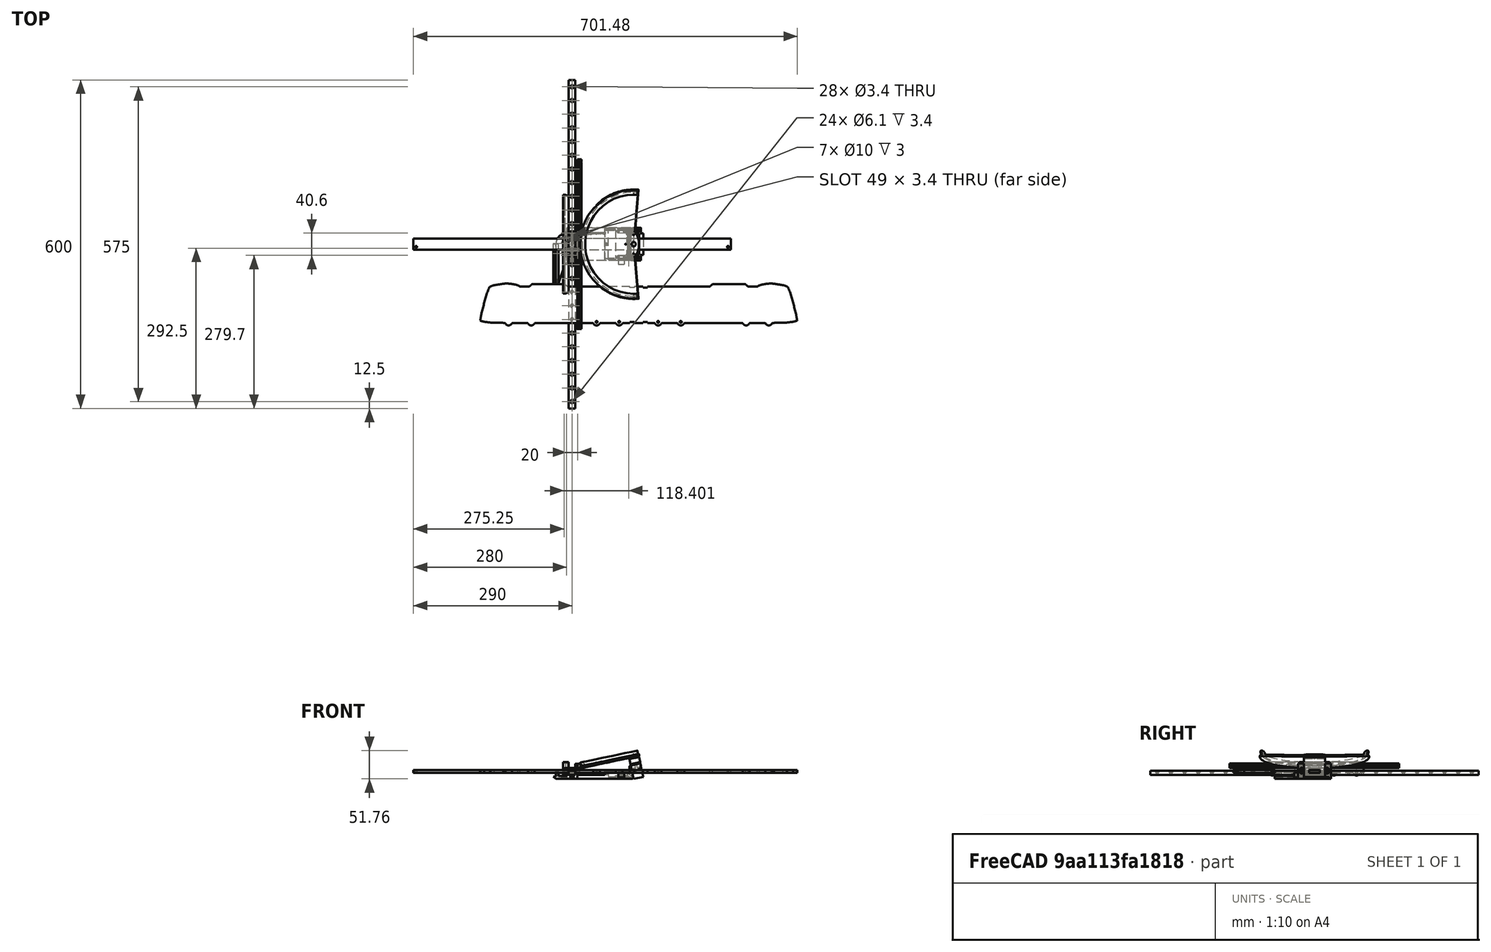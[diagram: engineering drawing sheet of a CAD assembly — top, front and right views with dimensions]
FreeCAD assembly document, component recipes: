
FREECAD ASSEMBLY — COMPONENT RECIPES ("mechanism")

This assembly document has 15 components, labeled P0..P14 below (a component is one placed body or linked part). 14 of them carry a construction recipe — the FreeCAD feature program that regenerates the part from scratch, quoted from this document or its linked companion documents; the rest are supplied as boundary geometry only. No exploded tour is included for this assembly.
NOTE — this tour is split across 2 documents so each fits a 32k-token context. This is document 1: the component sections continue in the remaining 1 document, each repeating the header above.
COMPONENT P0 — recipe-attached ("Block001", modeled in this document).
Construction recipe (the document's own serialized feature program — sketch geometry with constraints, then the solid features built on it; lengths are millimeters unless a unit is written):

FEATURE [PartDesign::SubShapeBinder] Binder  label="SubShapeBinder"
  BindCopyOnChange = 0
  BindMode = 0
  ClaimChildren = false
  Context = -> Body001 [Binder.]
  Fuse = false
  MakeFace = true
  OffsetFill = false
  OffsetIntersection = false
  OffsetJoinType = 0
  OffsetOpenResult = false
  PartialLoad = false
  Refine = true
  Relative = true
  Support = -> [Body[Sketch.]]
  _Version = 2
FEATURE [Sketcher::SketchObject] Sketch001  label="Block Cross-Section"
  ArcFitTolerance = 1e-06
  AttachmentSupport = -> [Binder]
  ExternalGeometry = -> [Binder]
  FullyConstrained = true
  MakeInternals = false
  MapMode = 5
  Placement = pos=(0,0,0) rot=(0,0.707107,0.707107;3.14159rad)
  sketch-geometry (17):
    g0: LineSegment StartX=-13.5 StartY=8.5 StartZ=0 EndX=-13.5 EndY=-0.5 EndZ=0
    g1: LineSegment StartX=-13 StartY=-1 StartZ=0 EndX=-6 EndY=-1 EndZ=0
    g2: LineSegment StartX=13.5 StartY=-0.5 StartZ=0 EndX=13.5 EndY=8.5 EndZ=0
    g3: LineSegment StartX=13 StartY=9 StartZ=0 EndX=-13 EndY=9 EndZ=0
    g4: GeomPoint [constr] X=0 Y=4 Z=0
    g5: LineSegment StartX=-6 StartY=-1 StartZ=0 EndX=-6 EndY=4 EndZ=0
    g6: LineSegment StartX=-6 StartY=4 StartZ=0 EndX=6 EndY=4 EndZ=0
    g7: LineSegment StartX=6 StartY=4 StartZ=0 EndX=6 EndY=-1 EndZ=0
    g8: LineSegment StartX=6 StartY=-1 StartZ=0 EndX=13 EndY=-1 EndZ=0
    g9: ArcOfCircle CenterX=-13 CenterY=8.5 CenterZ=0 NormalX=0 NormalY=0 NormalZ=1 AngleXU=0 Radius=0.5 StartAngle=1.5708 EndAngle=3.14159
    g10: GeomPoint [constr] X=-13.5 Y=9 Z=0
    g11: ArcOfCircle CenterX=13 CenterY=8.5 CenterZ=0 NormalX=0 NormalY=0 NormalZ=1 AngleXU=0 Radius=0.5 StartAngle=-1.8e-15 EndAngle=1.5708
    g12: GeomPoint [constr] X=13.5 Y=9 Z=0
    g13: ArcOfCircle CenterX=13 CenterY=-0.5 CenterZ=0 NormalX=0 NormalY=0 NormalZ=1 AngleXU=0 Radius=0.5 StartAngle=4.71239 EndAngle=6.28319
    g14: GeomPoint [constr] X=13.5 Y=-1 Z=0
    g15: ArcOfCircle CenterX=-13 CenterY=-0.5 CenterZ=0 NormalX=0 NormalY=0 NormalZ=1 AngleXU=0 Radius=0.5 StartAngle=3.14159 EndAngle=4.71239
    g16: GeomPoint [constr] X=-13.5 Y=-1 Z=0
  constraints (41):
    c: Vertical(g0)
    c: Vertical(g2)
    c: Horizontal(g1)
    c: Horizontal(g3)
    c: Symmetric(g14,g10,g4)
    c: PointOnObject(g4,g-2)
    c: Vertical(g5)
    c: Coincident(g5,g6)
    c: Coincident(g6,g7)
    c: PointOnObject(g7,g8)
    c: Vertical(g7)
    c: Coincident(g1,g5)
    c: PointOnObject(g8,g7)
    c: Symmetric(g6,g5,g-2)
    c: PointOnObject(g1,g-3)
    c: PointOnObject(g5,g-4)
    c: DistanceY(g-5,g10) = 13  'Height'
    c: DistanceY(g-5,g16) = 3  'H1'
    c: Horizontal(g7,g1)
    c: Horizontal(g8)
    c: DistanceX(g10,g12) = 27  'W'
    c: PointOnObject(g10,g0)
    c: PointOnObject(g10,g3)
    c: Tangent(g0,g9) = -1.5708
    c: Tangent(g3,g9) = -1.5708
    c: PointOnObject(g12,g3)
    c: PointOnObject(g12,g2)
    c: Tangent(g3,g11) = -1.5708
    c: Tangent(g2,g11) = -1.5708
    c: PointOnObject(g14,g8)
    c: PointOnObject(g14,g2)
    c: Tangent(g8,g13) = -1.5708
    c: Tangent(g2,g13) = -1.5708
    c: PointOnObject(g16,g1)
    c: PointOnObject(g16,g0)
    c: Tangent(g1,g15) = -1.5708
    c: Tangent(g0,g15) = -1.5708
    c: Equal(g9,g15)
    c: Equal(g15,g11)
    c: Equal(g11,g13)
    c: Radius(g9) = 0.5
FEATURE [PartDesign::Pad] Pad001
  Direction = (0,1,-2e-16)
  Length = 32.4
  Length2 = 10
  Midplane = true
  Profile = -> Sketch001
  ReferenceAxis = -> Sketch001 [N_Axis]
  Refine = true
  Suppressed = false
  Type = 0
FEATURE [Sketcher::SketchObject] Sketch002
  ArcFitTolerance = 1e-06
  AttachmentSupport = -> [XZ_Plane001]
  ExternalGeometry = -> [Sketch001]
  FullyConstrained = true
  MakeInternals = false
  MapMode = 5
  Placement = pos=(0,0,0) rot=(1,0,0;1.5708rad)
  sketch-geometry (8):
    g0: LineSegment StartX=-13 StartY=8.5 StartZ=0 EndX=-13 EndY=-0.5 EndZ=0
    g1: LineSegment StartX=-13 StartY=-0.5 StartZ=0 EndX=-6 EndY=-0.5 EndZ=0
    g2: LineSegment StartX=-6 StartY=-0.5 StartZ=0 EndX=-6 EndY=4 EndZ=0
    g3: LineSegment StartX=-6 StartY=4 StartZ=0 EndX=6 EndY=4 EndZ=0
    g4: LineSegment StartX=6 StartY=4 StartZ=0 EndX=6 EndY=-0.5 EndZ=0
    g5: LineSegment StartX=6 StartY=-0.5 StartZ=0 EndX=13 EndY=-0.5 EndZ=0
    g6: LineSegment StartX=13 StartY=-0.5 StartZ=0 EndX=13 EndY=8.5 EndZ=0
    g7: LineSegment StartX=13 StartY=8.5 StartZ=0 EndX=-13 EndY=8.5 EndZ=0
  constraints (22):
    c: Vertical(g0)
    c: Coincident(g0,g1)
    c: PointOnObject(g1,g-7)
    c: Horizontal(g1)
    c: Coincident(g1,g2)
    c: Coincident(g2,g-7)
    c: Coincident(g2,g3)
    c: Coincident(g3,g-6)
    c: Coincident(g3,g4)
    c: Coincident(g4,g5)
    c: Horizontal(g5)
    c: Coincident(g5,g6)
    c: Vertical(g6)
    c: Coincident(g6,g7)
    c: Coincident(g7,g0)
    c: Horizontal(g7)
    c: Vertical(g-3,g0)
    c: Horizontal(g0,g-4)
    c: Horizontal(g-4,g0)
    c: Vertical(g4)
    c: Horizontal(g5,g-5)
    c: Vertical(g-3,g6)
FEATURE [PartDesign::Pad] Pad002  label="BlockExtent"
  BaseFeature = -> Pad001
  Direction = (0,-1,2e-16)
  Length = 45.4
  Length2 = 10
  Midplane = true
  Profile = -> Sketch002
  ReferenceAxis = -> Sketch002 [N_Axis]
  Refine = true
  Suppressed = false
  Type = 0
FEATURE [Sketcher::SketchObject] Sketch004
  ArcFitTolerance = 1e-06
  AttachmentSupport = -> [Pad001]
  FullyConstrained = false
  MakeInternals = false
  MapMode = 5
  Placement = pos=(0,2e-15,9) rot=(0,0,1;0rad)
  sketch-geometry (9):
    g0: Circle CenterX=-10 CenterY=10 CenterZ=0 NormalX=0 NormalY=0 NormalZ=1 AngleXU=0 Radius=2.53403
    g1: Circle CenterX=10 CenterY=10 CenterZ=0 NormalX=0 NormalY=0 NormalZ=1 AngleXU=0 Radius=2.44373
    g2: Circle CenterX=-10 CenterY=-10 CenterZ=0 NormalX=0 NormalY=0 NormalZ=1 AngleXU=0 Radius=2.20024
    g3: Circle CenterX=10 CenterY=-10 CenterZ=0 NormalX=0 NormalY=0 NormalZ=1 AngleXU=0 Radius=2.23133
    g4: LineSegment [constr] StartX=-10 StartY=10 StartZ=0 EndX=-10 EndY=-10 EndZ=0
    g5: LineSegment [constr] StartX=-10 StartY=-10 StartZ=0 EndX=10 EndY=-10 EndZ=0
    g6: LineSegment [constr] StartX=10 StartY=-10 StartZ=0 EndX=10 EndY=10 EndZ=0
    g7: LineSegment [constr] StartX=10 StartY=10 StartZ=0 EndX=-10 EndY=10 EndZ=0
    g8: GeomPoint [constr] X=0 Y=0 Z=0
  constraints (16):
    c: Coincident(g4,g5)
    c: Coincident(g5,g6)
    c: Coincident(g6,g7)
    c: Coincident(g7,g4)
    c: Vertical(g4)
    c: Vertical(g6)
    c: Horizontal(g5)
    c: Horizontal(g7)
    c: Symmetric(g6,g4,g8)
    c: Coincident(g8,g-1)
    c: DistanceX(g7,g7) = 20  'B'
    c: DistanceY(g6,g6) = 20  'C'
    c: Coincident(g0,g4)
    c: Coincident(g1,g6)
    c: Coincident(g5,g3)
    c: Coincident(g4,g2)
FEATURE [PartDesign::Hole] Hole
  BaseFeature = -> Pad002
  CustomThreadClearance = 0
  Depth = 3.5
  DepthType = 0
  Diameter = 2.5
  DrillForDepth = false
  DrillPoint = 1
  DrillPointAngle = 118
  HoleCutCountersinkAngle = 90
  HoleCutCustomValues = false
  HoleCutDepth = 0
  HoleCutDiameter = 6.1
  HoleCutType = 0
  ModelThread = false
  Profile = -> Sketch004
  Refine = true
  Suppressed = false
  Tapered = false
  TaperedAngle = 90
  ThreadClass = 0
  ThreadDepth = 3.5
  ThreadDepthType = 0
  ThreadDirection = 0
  ThreadFit = 0
  ThreadSize = 9
  ThreadType = 1
  Threaded = true
  UseCustomThreadClearance = false
FEATURE [PartDesign::Body] Body001  label="Block"
  AllowCompound = false
  Group = -> [Binder,Sketch001,Pad001,Sketch002,Pad002,Sketch004,Hole]
  Origin = -> Origin001
  Tip = -> Hole
COMPONENT P1 — recipe-attached ("CountdownBracket001", modeled in this document).
Construction recipe (the document's own serialized feature program — sketch geometry with constraints, then the solid features built on it; lengths are millimeters unless a unit is written):

FEATURE [PartDesign::FeatureBase] Clone
  BaseFeature = -> Mirrored
  Placement = pos=(0,0,0) rot=(1,0,0;1.5708rad)
  Suppressed = false
FEATURE [Sketcher::SketchObject] Sketch056
  ArcFitTolerance = 1e-06
  AttachmentSupport = -> [XZ_Plane012]
  FullyConstrained = true
  MakeInternals = false
  MapMode = 5
  Placement = pos=(0,0,0) rot=(1,0,0;1.5708rad)
  sketch-geometry (10):
    g0: LineSegment StartX=-1.7 StartY=-5.97022 StartZ=0 EndX=-2.9 EndY=-6.52978 EndZ=0
    g1: LineSegment StartX=-2.9 StartY=-6.52978 StartZ=0 EndX=-2.9 EndY=-9.02978 EndZ=0
    g2: LineSegment StartX=-2.9 StartY=-9.02978 StartZ=0 EndX=-1.7 EndY=-9.02978 EndZ=0
    g3: LineSegment StartX=1.7 StartY=-9.02978 StartZ=0 EndX=2.9 EndY=-9.02978 EndZ=0
    g4: LineSegment StartX=2.9 StartY=-9.02978 StartZ=0 EndX=2.9 EndY=-6.52978 EndZ=0
    g5: LineSegment StartX=2.9 StartY=-6.52978 StartZ=0 EndX=1.7 EndY=-5.97022 EndZ=0
    g6: LineSegment StartX=1.7 StartY=-5.97022 StartZ=0 EndX=-1.7 EndY=-5.97022 EndZ=0
    g7: LineSegment StartX=-1.7 StartY=-9.02978 StartZ=0 EndX=1.7 EndY=-9.02978 EndZ=0
    g8: LineSegment [constr] StartX=1.7 StartY=-5.97022 StartZ=0 EndX=1.7 EndY=-4 EndZ=0
    g9: LineSegment [constr] StartX=1.7 StartY=-9.02978 StartZ=0 EndX=1.7 EndY=-11 EndZ=0
  constraints (28):
    c: PointOnObject(g0,g-3)
    c: Coincident(g0,g1)
    c: Vertical(g1)
    c: Coincident(g1,g2)
    c: Horizontal(g2)
    c: PointOnObject(g2,g-3)
    c: PointOnObject(g3,g-4)
    c: Horizontal(g3)
    c: Coincident(g3,g4)
    c: Vertical(g4)
    c: Coincident(g4,g5)
    c: PointOnObject(g5,g-4)
    c: Coincident(g5,g6)
    c: Coincident(g6,g0)
    c: Horizontal(g6)
    c: Horizontal(g2,g3)
    c: Equal(g1,g4)
    c: Equal(g0,g5)
    c: Angle(g-4,g5) = 1.13446
    c: DistanceY(g1,g1) = 2.5
    c: Distance(g4,g1) = 5.8
    c: Coincident(g7,g2)
    c: Coincident(g7,g3)
    c: Coincident(g8,g5)
    c: Coincident(g8,g-4)
    c: Coincident(g9,g3)
    c: Coincident(g9,g-4)
    c: Equal(g9,g8)
FEATURE [PartDesign::SubShapeBinder] Binder024  label="CarriageBinder"
  BindCopyOnChange = 0
  BindMode = 0
  ClaimChildren = false
  Context = -> Body011 [Binder024.]
  Fuse = false
  MakeFace = true
  OffsetFill = false
  OffsetIntersection = false
  OffsetJoinType = 0
  OffsetOpenResult = false
  PartialLoad = false
  Refine = true
  Relative = true
  Support = -> [Body003[Pocket.Face11]]
  _Version = 2
FEATURE [PartDesign::SubShapeBinder] Binder025  label="TramBinder"
  BindCopyOnChange = 0
  BindMode = 0
  ClaimChildren = false
  Context = -> Body011 [Binder025.]
  Fuse = false
  MakeFace = true
  OffsetFill = false
  OffsetIntersection = false
  OffsetJoinType = 0
  OffsetOpenResult = false
  PartialLoad = false
  Placement = pos=(0,-217,0) rot=(0,0,1;0rad)
  Refine = true
  Relative = true
  Support = -> [Body003[Sketch052.]]
  _Version = 2
FEATURE [Sketcher::SketchObject] Sketch057  label="CountdownShapeBack"
  ArcFitTolerance = 1e-06
  AttachmentOffset = pos=(0,0,13) rot=(0,0,1;0rad)
  AttachmentSupport = -> [Binder024]
  ExternalGeometry = -> [Binder025]
  FullyConstrained = true
  MakeInternals = false
  MapMode = 5
  Placement = pos=(-29.5,0,0) rot=(0.57735,-0.57735,-0.57735;2.0944rad)
  sketch-geometry (5):
    g0: LineSegment StartX=-72.6664 StartY=12.9462 StartZ=0 EndX=-72.6664 EndY=-7.05384 EndZ=0
    g1: LineSegment StartX=-72.6664 StartY=-7.05384 StartZ=0 EndX=507.334 EndY=-7.05384 EndZ=0
    g2: LineSegment StartX=507.334 StartY=-7.05384 StartZ=0 EndX=507.334 EndY=12.9462 EndZ=0
    g3: LineSegment StartX=507.334 StartY=12.9462 StartZ=0 EndX=-72.6664 EndY=12.9462 EndZ=0
    g4: Circle CenterX=-67.6664 CenterY=-2.05384 CenterZ=0 NormalX=0 NormalY=0 NormalZ=1 AngleXU=0 Radius=1.7
  constraints (15):
    c: Coincident(g0,g1)
    c: Coincident(g1,g2)
    c: Coincident(g2,g3)
    c: Coincident(g3,g0)
    c: Vertical(g0)
    c: Vertical(g2)
    c: Horizontal(g1)
    c: Horizontal(g3)
    c: Distance(g0,g0) = 20
    c: DistanceX(g3,g3) = 580
    c: PointOnObject(g-3,g3)
    c: PointOnObject(g-4,g0)
    c: Diameter(g4) = 3.4
    c: Distance(g4,g0) = 5
    c: Distance(g4,g1) = 5
FEATURE [PartDesign::Pad] Pad024
  BaseFeature = -> Clone
  Direction = (0,1,-3e-16)
  Length = 30
  Length2 = 10
  Placement = pos=(0,0,0) rot=(1,0,0;1.5708rad)
  Profile = -> Clone [Face12]
  Refine = true
  Suppressed = false
  Type = 0
FEATURE [Sketcher::SketchObject] Sketch055
  ArcFitTolerance = 1e-06
  AttachmentSupport = -> [Pad024]
  ExternalGeometry = -> [Pad024]
  FullyConstrained = true
  MakeInternals = false
  MapMode = 5
  Placement = pos=(0,-1.9e-15,-4) rot=(0,0,1;3.14159rad)
  sketch-geometry (6):
    g0: ArcOfCircle CenterX=0 CenterY=15.3 CenterZ=0 NormalX=0 NormalY=0 NormalZ=1 AngleXU=0 Radius=1.7 StartAngle=0 EndAngle=3.14159
    g1: ArcOfCircle CenterX=1.07e-14 CenterY=-30.3 CenterZ=0 NormalX=0 NormalY=0 NormalZ=1 AngleXU=0 Radius=1.7 StartAngle=3.14159 EndAngle=6.28319
    g2: LineSegment StartX=1.7 StartY=15.3 StartZ=0 EndX=1.7 EndY=-30.3 EndZ=0
    g3: LineSegment StartX=-1.7 StartY=15.3 StartZ=0 EndX=-1.7 EndY=-30.3 EndZ=0
    g4: GeomPoint X=0 Y=17 Z=0
    g5: GeomPoint X=0 Y=-32 Z=0
  constraints (14):
    c: Tangent(g0,g2) = 1.5708
    c: Tangent(g0,g3) = -1.5708
    c: Tangent(g1,g2) = 1.5708
    c: Tangent(g1,g3) = -1.5708
    c: Equal(g0,g1)
    c: Vertical(g3)
    c: PointOnObject(g0,g-2)
    c: Diameter(g0) = 3.4
    c: PointOnObject(g4,g0)
    c: PointOnObject(g5,g1)
    c: PointOnObject(g4,g-2)
    c: PointOnObject(g5,g-2)
    c: Distance(g4,g-3) = 3
    c: Distance(g5,g-4) = 3
FEATURE [PartDesign::Pocket] Pocket018  label="ScrewSlot"
  BaseFeature = -> Pad024
  Direction = (0,0,-1)
  Length = 5
  Length2 = 5
  Placement = pos=(0,0,0) rot=(1,0,0;1.5708rad)
  Profile = -> Sketch055
  ReferenceAxis = -> Sketch055 [N_Axis]
  Refine = true
  Suppressed = false
  Type = 1
FEATURE [PartDesign::Pocket] Pocket019  label="NutSlot"
  BaseFeature = -> Pocket018
  Direction = (0,1,-2e-16)
  Length = 0
  Length2 = 5
  Midplane = true
  Placement = pos=(0,0,0) rot=(1,0,0;1.5708rad)
  Profile = -> Sketch056
  ReferenceAxis = -> Sketch056 [N_Axis]
  Refine = true
  Suppressed = false
  Type = 1
FEATURE [Sketcher::SketchObject] Sketch058
  ArcFitTolerance = 1e-06
  AttachmentSupport = -> [Pocket019]
  ExternalGeometry = -> [Sketch057,Binder025,Pocket019]
  FullyConstrained = true
  MakeInternals = false
  MapMode = 5
  Placement = pos=(0,-5.4e-15,-11) rot=(1,0,0;3.14159rad)
  sketch-geometry (11):
    g0: LineSegment StartX=-29.5 StartY=-72.6664 StartZ=0 EndX=-26.4004 EndY=-72.6664 EndZ=0
    g1: LineSegment StartX=-29.5 StartY=-72.6664 StartZ=0 EndX=-29.5 EndY=0.2 EndZ=0
    g2: ArcOfCircle CenterX=-9.7 CenterY=0.2 CenterZ=0 NormalX=0 NormalY=0 NormalZ=1 AngleXU=0 Radius=19.8 StartAngle=1.5708 EndAngle=3.14159
    g3: ArcOfCircle CenterX=-26.4004 CenterY=-70.6664 CenterZ=0 NormalX=0 NormalY=0 NormalZ=1 AngleXU=0 Radius=2 StartAngle=4.71239 EndAngle=5.96626
    g4: LineSegment StartX=-24.5 StartY=-71.2897 StartZ=0 EndX=-13.5008 EndY=-37.7534 EndZ=0
    g5: ArcOfCircle CenterX=-9.7 CenterY=-39 CenterZ=0 NormalX=0 NormalY=0 NormalZ=1 AngleXU=0 Radius=4 StartAngle=1.5708 EndAngle=2.82467
    g6: LineSegment [constr] StartX=-16.5 StartY=-72.6664 StartZ=0 EndX=-16.5 EndY=74.3613 EndZ=0
    g7: LineSegment [constr] StartX=-16.5 StartY=74.3613 StartZ=0 EndX=-21.5 EndY=74.3613 EndZ=0
    g8: LineSegment [constr] StartX=-21.5 StartY=74.3613 StartZ=0 EndX=-21.5 EndY=-72.6664 EndZ=0
    g9: LineSegment [constr] StartX=-21.5 StartY=-72.6664 StartZ=0 EndX=-16.5 EndY=-72.6664 EndZ=0
    g10: LineSegment StartX=-9.7 StartY=20 StartZ=0 EndX=-9.7 EndY=-35 EndZ=0
  constraints (27):
    c: Coincident(g0,g-4)
    c: Horizontal(g0)
    c: Coincident(g1,g0)
    c: Tangent(g1,g2) = 1.5708
    c: Tangent(g0,g3) = -1.5708
    c: Radius(g3) = 2
    c: DistanceX(g0,g3) = 5
    c: PointOnObject(g1,g-4)
    c: Tangent(g5,g4) = 1.5708
    c: Coincident(g6,g7)
    c: Coincident(g7,g8)
    c: Coincident(g8,g9)
    c: Coincident(g9,g6)
    c: Vertical(g8)
    c: Horizontal(g7)
    c: Horizontal(g9)
    c: Distance(g6,g8) = 5
    c: Coincident(g6,g-5)
    c: Coincident(g6,g-6)
    c: Tangent(g4,g3) = -1.5708
    c: Radius(g5) = 4
    c: Coincident(g-7,g2)
    c: PointOnObject(g2,g-7)
    c: Coincident(g5,g-7)
    c: Vertical(g5,g5)
    c: Coincident(g10,g5)
    c: Coincident(g2,g10)
FEATURE [PartDesign::Pad] Pad021  label="Arm"
  BaseFeature = -> Pocket019
  Direction = (0,0,-1)
  Length = 10
  Length2 = 10
  Placement = pos=(0,0,0) rot=(1,0,0;1.5708rad)
  Profile = -> Sketch058
  ReferenceAxis = -> Sketch058 [N_Axis]
  Refine = true
  Suppressed = false
  Type = 3
  UpToFace = -> Pocket019 [Face18]
FEATURE [Sketcher::SketchObject] Sketch059
  ArcFitTolerance = 1e-06
  AttachmentSupport = -> [Pad021]
  ExternalGeometry = -> [Pad021]
  FullyConstrained = true
  MakeInternals = false
  MapMode = 5
  Placement = pos=(0,-2.6e-15,-5.97022) rot=(0,0,1;3.14159rad)
  sketch-geometry (7):
    g0: LineSegment StartX=29.5 StartY=0.2 StartZ=0 EndX=29.5 EndY=-72.6664 EndZ=0
    g1: LineSegment StartX=29.5 StartY=-72.6664 StartZ=0 EndX=26.4004 EndY=-72.6664 EndZ=0
    g2: LineSegment StartX=24.5 StartY=-71.2897 StartZ=0 EndX=24.5 EndY=-1.8 EndZ=0
    g3: LineSegment StartX=26.5 StartY=0.2 StartZ=0 EndX=29.5 EndY=0.2 EndZ=0
    g4: ArcOfCircle CenterX=26.4004 CenterY=-70.6664 CenterZ=0 NormalX=0 NormalY=0 NormalZ=1 AngleXU=0 Radius=2 StartAngle=3.45852 EndAngle=4.71239
    g5: ArcOfCircle CenterX=26.5 CenterY=-1.8 CenterZ=0 NormalX=0 NormalY=0 NormalZ=1 AngleXU=0 Radius=2 StartAngle=1.5708 EndAngle=3.14159
    g6: GeomPoint [constr] X=24.5 Y=0.2 Z=0
  constraints (17):
    c: Coincident(g0,g1)
    c: Vertical(g2)
    c: Coincident(g3,g0)
    c: Horizontal(g3)
    c: Coincident(g4,g1)
    c: Coincident(g4,g2)
    c: PointOnObject(g6,g2)
    c: PointOnObject(g6,g3)
    c: Tangent(g2,g5) = 1.5708
    c: Tangent(g3,g5) = 1.5708
    c: Equal(g5,g4)
    c: Vertical(g0)
    c: Horizontal(g1)
    c: Equal(g4,g-4)
    c: Coincident(g1,g-4)
    c: Coincident(g2,g-4)
    c: Coincident(g0,g-3)
FEATURE [PartDesign::Pad] Pad022
  BaseFeature = -> Pad021
  Direction = (0,0,1)
  Length = 9
  Length2 = 10
  Placement = pos=(0,0,0) rot=(1,0,0;1.5708rad)
  Profile = -> Sketch059
  ReferenceAxis = -> Sketch059 [N_Axis]
  Refine = true
  Suppressed = false
  Type = 0
FEATURE [Sketcher::SketchObject] Sketch060
  ArcFitTolerance = 1e-06
  AttachmentSupport = -> [Pad022]
  ExternalGeometry = -> [Sketch057]
  FullyConstrained = true
  MakeInternals = false
  MapMode = 5
  Placement = pos=(-29.5,0,0) rot=(0.707107,0,-0.707107;3.14159rad)
  sketch-geometry (1):
    g0: Circle CenterX=2.05384 CenterY=-67.6664 CenterZ=0 NormalX=0 NormalY=0 NormalZ=1 AngleXU=0 Radius=1.7
  constraints (2):
    c: Coincident(g0,g-3)
    c: Equal(g0,g-3)
FEATURE [PartDesign::Hole] Hole012
  BaseFeature = -> Pad022
  CustomThreadClearance = 0
  Depth = 222.393
  DepthType = 1
  Diameter = 3.4
  DrillForDepth = false
  DrillPoint = 1
  DrillPointAngle = 118
  HoleCutCountersinkAngle = 90
  HoleCutCustomValues = false
  HoleCutDepth = 0
  HoleCutDiameter = 6.1
  HoleCutType = 0
  ModelThread = false
  Placement = pos=(0,0,0) rot=(1,0,0;1.5708rad)
  Profile = -> Sketch060
  Refine = true
  Suppressed = false
  Tapered = false
  TaperedAngle = 90
  ThreadClass = 0
  ThreadDepth = 222.393
  ThreadDepthType = 0
  ThreadDirection = 0
  ThreadFit = 0
  ThreadSize = 9
  ThreadType = 1
  Threaded = false
  UseCustomThreadClearance = false
FEATURE [Sketcher::SketchObject] Sketch061
  ArcFitTolerance = 1e-06
  AttachmentSupport = -> [Hole012]
  ExternalGeometry = -> [Sketch057]
  FullyConstrained = true
  MakeInternals = false
  MapMode = 5
  Placement = pos=(0,72.6664,0) rot=(-1,0,0;1.5708rad)
  sketch-geometry (3):
    g0: LineSegment StartX=-29.5 StartY=11 StartZ=0 EndX=-34 EndY=7.05384 EndZ=0
    g1: LineSegment StartX=-34 StartY=7.05384 StartZ=0 EndX=-29.5 EndY=7.05384 EndZ=0
    g2: LineSegment StartX=-29.5 StartY=11 StartZ=0 EndX=-29.5 EndY=7.05384 EndZ=0
  constraints (9):
    c: Coincident(g-3,g0)
    c: Coincident(g0,g1)
    c: PointOnObject(g1,g-3)
    c: Horizontal(g1)
    c: Distance(g1,g1) = 4.5
    c: Angle(g0,g-3) = 0.850877
    c: PointOnObject(g-4,g1)
    c: Coincident(g2,g0)
    c: Coincident(g2,g1)
FEATURE [PartDesign::Pad] Pad023
  BaseFeature = -> Hole012
  Direction = (0,1,2e-16)
  Length = 10
  Length2 = 10
  Placement = pos=(0,0,0) rot=(1,0,0;1.5708rad)
  Profile = -> Sketch061
  ReferenceAxis = -> Sketch061 [N_Axis]
  Refine = true
  Reversed = true
  Suppressed = false
  Type = 3
  UpToFace = -> Hole012 [Face37]
FEATURE [Sketcher::SketchObject] Sketch062
  ArcFitTolerance = 1e-06
  AttachmentSupport = -> [Pad023]
  ExternalGeometry = -> [Pad023]
  FullyConstrained = true
  MakeInternals = false
  MapMode = 5
  Placement = pos=(-24.5,0,0) rot=(0.707107,0,0.707107;3.14159rad)
  sketch-geometry (7):
    g0: LineSegment StartX=-3.78589 StartY=-64.6664 StartZ=0 EndX=-5.51794 EndY=-67.6664 EndZ=0
    g1: LineSegment StartX=-5.51794 StartY=-67.6664 StartZ=0 EndX=-3.78589 EndY=-70.6664 EndZ=0
    g2: LineSegment StartX=-3.78589 StartY=-70.6664 StartZ=0 EndX=-0.321787 EndY=-70.6664 EndZ=0
    g3: LineSegment StartX=-0.321787 StartY=-70.6664 StartZ=0 EndX=1.41026 EndY=-67.6664 EndZ=0
    g4: LineSegment StartX=1.41026 StartY=-67.6664 StartZ=0 EndX=-0.321787 EndY=-64.6664 EndZ=0
    g5: LineSegment StartX=-0.321787 StartY=-64.6664 StartZ=0 EndX=-3.78589 EndY=-64.6664 EndZ=0
    g6: Circle [constr] CenterX=-2.05384 CenterY=-67.6664 CenterZ=0 NormalX=0 NormalY=0 NormalZ=1 AngleXU=0 Radius=3.4641
  constraints (16):
    c: Coincident(g0,g1)
    c: Coincident(g1,g2)
    c: Coincident(g2,g3)
    c: Coincident(g3,g4)
    c: Coincident(g4,g5)
    c: Coincident(g5,g0)
    c: Equal(g0, g1-g5) x5
    c: PointOnObject(g0,g6)
    c: PointOnObject(g1,g6)
    c: PointOnObject(g2,g6)
    c: PointOnObject(g3,g6)
    c: PointOnObject(g4,g6)
    c: PointOnObject(g5,g6)
    c: Coincident(g6,g-3)
    c: Horizontal(g5)
    c: Distance(g2,g5) = 6
FEATURE [PartDesign::Pocket] Pocket020  label="HexNutHole"
  BaseFeature = -> Pad023
  Direction = (-1,0,2e-16)
  Length = 2.5
  Length2 = 5
  Placement = pos=(0,0,0) rot=(1,0,0;1.5708rad)
  Profile = -> Sketch062
  ReferenceAxis = -> Sketch062 [N_Axis]
  Refine = true
  Suppressed = false
  Type = 0
FEATURE [Sketcher::SketchObject] Sketch063
  ArcFitTolerance = 1e-06
  AttachmentSupport = -> [Pocket020]
  ExternalGeometry = -> [Pocket020]
  FullyConstrained = true
  MakeInternals = false
  MapMode = 5
  Placement = pos=(0,-3.2e-15,-11) rot=(1,0,0;3.14159rad)
  expr: Constraints[0] = <<FootPads>>.Constraints.FootDiameter
  sketch-geometry (7):
    g0: Circle CenterX=-14.75 CenterY=1.23011 CenterZ=0 NormalX=0 NormalY=0 NormalZ=1 AngleXU=0 Radius=5
    g1: LineSegment [constr] StartX=-29.5 StartY=0.2 StartZ=0 EndX=0 EndY=0.2 EndZ=0
    g2: Circle CenterX=-14.75 CenterY=-16.8849 CenterZ=0 NormalX=0 NormalY=0 NormalZ=1 AngleXU=0 Radius=5
    g3: GeomPoint X=-14.75 Y=0.2 Z=0
    g4: LineSegment [constr] StartX=-14.75 StartY=1.23011 StartZ=0 EndX=-14.75 EndY=19.3452 EndZ=0
    g5: LineSegment [constr] StartX=-14.75 StartY=1.23011 StartZ=0 EndX=-14.75 EndY=-16.8849 EndZ=0
    g6: LineSegment [constr] StartX=-14.75 StartY=-16.8849 StartZ=0 EndX=-14.75 EndY=-35 EndZ=0
  constraints (18):
    c: Diameter(g0) = 10
    c: Horizontal(g1)
    c: PointOnObject(g1,g-2)
    c: Symmetric(g1,g1,g3)
    c: Vertical(g3,g2)
    c: Vertical(g0,g3)
    c: Equal(g0,g2)
    c: Coincident(g4,g0)
    c: Vertical(g4)
    c: Coincident(g5,g0)
    c: Coincident(g5,g2)
    c: Coincident(g6,g2)
    c: Vertical(g6)
    c: Equal(g6,g5)
    c: Equal(g6,g4)
    c: Horizontal(g6,g-4)
    c: PointOnObject(g4,g-3)
    c: Coincident(g1,g-3)
FEATURE [PartDesign::Pocket] Pocket021  label="FootPad"
  BaseFeature = -> Pocket020
  Direction = (0,0,1)
  Length = 3
  Length2 = 5
  Placement = pos=(0,0,0) rot=(1,0,0;1.5708rad)
  Profile = -> Sketch063
  ReferenceAxis = -> Sketch063 [N_Axis]
  Refine = true
  Suppressed = false
  Type = 0
  expr: Length = <<FootPadPocket>>.Length
FEATURE [PartDesign::Body] Body011  label="CountdownBracketL"
  AllowCompound = false
  Group = -> [Clone,Pad024,Sketch055,Pocket018,Sketch056,Pocket019,Binder024,Sketch057,Binder025,Sketch058,Pad021,Sketch059,Pad022,Sketch060,Hole012,Sketch061,Pad023,Sketch062,Pocket020,Sketch063,Pocket021]
  Origin = -> Origin012
  Tip = -> Pocket021
COMPONENT P2 — geometry summary ("CountdownBracketOtherEnd001"; no construction recipe available for this part):
  bounding box: 92.7 x 43.7 x 14.0 mm
  tessellated surface: 2,048 triangles
  volume: 16868 mm^3 (30% of its bounding box)
COMPONENT P3 — recipe-attached ("CountdownPlaceholder001", modeled in this document).
Construction recipe (the document's own serialized feature program — sketch geometry with constraints, then the solid features built on it; lengths are millimeters unless a unit is written):

FEATURE [Sketcher::SketchObject] Sketch067
  ArcFitTolerance = 1e-06
  AttachmentSupport = -> [XY_Plane015]
  FullyConstrained = true
  MakeInternals = false
  MapMode = 5
  sketch-geometry (15):
    g0: LineSegment StartX=-290 StartY=-10 StartZ=0 EndX=290 EndY=-10 EndZ=0
    g1: LineSegment StartX=290 StartY=-10 StartZ=0 EndX=290 EndY=10 EndZ=0
    g2: LineSegment StartX=290 StartY=10 StartZ=0 EndX=-290 EndY=10 EndZ=0
    g3: LineSegment StartX=-290 StartY=10 StartZ=0 EndX=-290 EndY=-10 EndZ=0
    g4: GeomPoint [constr] X=0 Y=0 Z=0
    g5: LineSegment [constr] StartX=-290 StartY=-10 StartZ=0 EndX=-285 EndY=-10 EndZ=0
    g6: LineSegment [constr] StartX=-285 StartY=-10 StartZ=0 EndX=-285 EndY=-5 EndZ=0
    g7: LineSegment [constr] StartX=-285 StartY=-5 StartZ=0 EndX=-290 EndY=-5 EndZ=0
    g8: LineSegment [constr] StartX=-290 StartY=-5 StartZ=0 EndX=-290 EndY=-10 EndZ=0
    g9: LineSegment [constr] StartX=290 StartY=-10 StartZ=0 EndX=290 EndY=-5 EndZ=0
    g10: LineSegment [constr] StartX=290 StartY=-5 StartZ=0 EndX=285 EndY=-5 EndZ=0
    g11: LineSegment [constr] StartX=285 StartY=-5 StartZ=0 EndX=285 EndY=-10 EndZ=0
    g12: LineSegment [constr] StartX=285 StartY=-10 StartZ=0 EndX=290 EndY=-10 EndZ=0
    g13: Circle CenterX=-285 CenterY=-5 CenterZ=0 NormalX=0 NormalY=0 NormalZ=1 AngleXU=0 Radius=1.75
    g14: Circle CenterX=285 CenterY=-5 CenterZ=0 NormalX=0 NormalY=0 NormalZ=1 AngleXU=0 Radius=1.75
  constraints (38):
    c: Coincident(g0,g1)
    c: Coincident(g1,g2)
    c: Coincident(g2,g3)
    c: Coincident(g3,g0)
    c: Horizontal(g0)
    c: Horizontal(g2)
    c: Vertical(g1)
    c: Vertical(g3)
    c: Symmetric(g2,g0,g4)
    c: Distance(g1,g3) = 580
    c: Distance(g0,g2) = 20
    c: Coincident(g4,g-1)
    c: Coincident(g5,g6)
    c: Coincident(g6,g7)
    c: Coincident(g7,g8)
    c: Coincident(g8,g5)
    c: Horizontal(g5)
    c: Horizontal(g7)
    c: Vertical(g6)
    c: Vertical(g8)
    c: Distance(g6,g8) = 5
    c: Distance(g5,g7) = 5
    c: Coincident(g5,g0)
    c: Coincident(g9,g10)
    c: Coincident(g10,g11)
    c: Coincident(g11,g12)
    c: Coincident(g12,g9)
    c: Vertical(g9)
    c: Vertical(g11)
    c: Horizontal(g10)
    c: Horizontal(g12)
    c: Distance(g9,g11) = 5
    c: Distance(g10,g12) = 5
    c: Coincident(g9,g0)
    c: Diameter(g13) = 3.5
    c: Coincident(g13,g6)
    c: Diameter(g14) = 3.5
    c: Coincident(g14,g10)
FEATURE [PartDesign::Pad] Pad026
  Direction = (0,0,1)
  Length = 5
  Length2 = 10
  Profile = -> Sketch067
  ReferenceAxis = -> Sketch067 [N_Axis]
  Refine = true
  Suppressed = false
  Type = 0
FEATURE [PartDesign::Body] Body013  label="CountdownPlaceholder"
  AllowCompound = false
  Group = -> [Sketch067,Pad026]
  Origin = -> Origin015
  Tip = -> Pad026
COMPONENT P4 — recipe-attached ("ElectronicsLid001", modeled in this document).
Construction recipe (the document's own serialized feature program — sketch geometry with constraints, then the solid features built on it; lengths are millimeters unless a unit is written):

FEATURE [PartDesign::SubShapeBinder] Binder018
  BindCopyOnChange = 0
  BindMode = 0
  ClaimChildren = false
  Context = -> Body009 [Binder018.]
  Fuse = false
  MakeFace = true
  OffsetFill = false
  OffsetIntersection = false
  OffsetJoinType = 0
  OffsetOpenResult = false
  PartialLoad = false
  Refine = true
  Relative = true
  Support = -> [Body006[Sketch042.]]
  _Version = 2
FEATURE [PartDesign::SubShapeBinder] Binder019
  BindCopyOnChange = 0
  BindMode = 0
  ClaimChildren = false
  Context = -> Body009 [Binder019.]
  Fuse = false
  MakeFace = true
  OffsetFill = false
  OffsetIntersection = false
  OffsetJoinType = 0
  OffsetOpenResult = false
  PartialLoad = false
  Refine = true
  Relative = true
  Support = -> [Body006[Sketch023.]]
  _Version = 2
FEATURE [Sketcher::SketchObject] Sketch046
  ArcFitTolerance = 1e-06
  AttachmentSupport = -> [Binder018]
  ExternalGeometry = -> [Binder018]
  FullyConstrained = true
  MakeInternals = false
  MapMode = 5
  Placement = pos=(100.82,0,0) rot=(0.57735,0.57735,0.57735;2.0944rad)
  sketch-geometry (4):
    g0: LineSegment StartX=-25.8 StartY=4 StartZ=0 EndX=-27.8 EndY=2 EndZ=0
    g1: LineSegment StartX=-27.8 StartY=2 StartZ=0 EndX=27.8 EndY=2 EndZ=0
    g2: LineSegment StartX=27.8 StartY=2 StartZ=0 EndX=25.8 EndY=4 EndZ=0
    g3: LineSegment StartX=25.8 StartY=4 StartZ=0 EndX=-25.8 EndY=4 EndZ=0
  constraints (11):
    c: PointOnObject(g0,g-3)
    c: PointOnObject(g0,g-5)
    c: Coincident(g0,g1)
    c: PointOnObject(g1,g-5)
    c: Coincident(g1,g2)
    c: Coincident(g2,g3)
    c: Coincident(g3,g0)
    c: Equal(g-4,g0)
    c: Equal(g-6,g2)
    c: Symmetric(g0,g2,g-2)
    c: Distance(g2,g-6) = 0.2
FEATURE [PartDesign::Pad] Pad018
  Direction = (1,0,0)
  Length = 1.9
  Length2 = 10
  Profile = -> Sketch046
  ReferenceAxis = -> Sketch046 [N_Axis]
  Refine = true
  Suppressed = false
  Type = 0
  expr: Length = <<LidOvershoot>>.Length - 0.1 mm
FEATURE [PartDesign::SubShapeBinder] Binder020
  BindCopyOnChange = 0
  BindMode = 0
  ClaimChildren = false
  Context = -> Body009 [Binder020.]
  Fuse = false
  MakeFace = true
  OffsetFill = false
  OffsetIntersection = false
  OffsetJoinType = 0
  OffsetOpenResult = false
  PartialLoad = false
  Refine = true
  Relative = true
  Support = -> [Body006[SubtractivePipe.Face17]]
  _Version = 2
FEATURE [PartDesign::Pad] Pad019
  BaseFeature = -> Pad018
  Direction = (1,0,0)
  Length = 10
  Length2 = 10
  Profile = -> Sketch046
  ReferenceAxis = -> Sketch046 [N_Axis]
  Refine = true
  Suppressed = false
  Type = 3
  UpToFace = -> SubtractivePipe [Face17]
FEATURE [PartDesign::SubShapeBinder] Binder022
  BindCopyOnChange = 0
  BindMode = 0
  ClaimChildren = false
  Context = -> Body009 [Binder022.]
  Fuse = false
  MakeFace = true
  OffsetFill = false
  OffsetIntersection = false
  OffsetJoinType = 0
  OffsetOpenResult = false
  PartialLoad = false
  Refine = true
  Relative = true
  Support = -> [Body006[Sketch049.]]
  _Version = 2
FEATURE [Sketcher::SketchObject] Sketch047
  ArcFitTolerance = 1e-06
  AttachmentSupport = -> [Binder019]
  ExternalGeometry = -> [Binder019,Binder022]
  FullyConstrained = true
  MakeInternals = false
  MapMode = 5
  Placement = pos=(0,-6e-16,0) rot=(0,0.707107,0.707107;3.14159rad)
  sketch-geometry (7):
    g0: LineSegment StartX=-61.8197 StartY=4 StartZ=0 EndX=-59.8197 EndY=4 EndZ=0
    g1: LineSegment StartX=-59.8197 StartY=4 StartZ=0 EndX=-59.8197 EndY=2 EndZ=0
    g2: ArcOfCircle CenterX=-61.8197 CenterY=2 CenterZ=0 NormalX=0 NormalY=0 NormalZ=1 AngleXU=0 Radius=2 StartAngle=9.81107e-09 EndAngle=1.5708
    g3: LineSegment StartX=-102.82 StartY=2 StartZ=0 EndX=-102.82 EndY=4 EndZ=0
    g4: LineSegment StartX=-102.82 StartY=4 StartZ=0 EndX=-101.55 EndY=4 EndZ=0
    g5: LineSegment StartX=-101.55 StartY=4 StartZ=0 EndX=-102.704 EndY=2 EndZ=0
    g6: LineSegment StartX=-102.704 StartY=2 StartZ=0 EndX=-102.82 EndY=2 EndZ=0
  constraints (18):
    c: Coincident(g-3,g0)
    c: Coincident(g0,g1)
    c: Coincident(g1,g-3)
    c: Vertical(g1)
    c: Horizontal(g0)
    c: Coincident(g2,g0)
    c: Coincident(g2,g1)
    c: Tangent(g2,g-3)
    c: Coincident(g-5,g3)
    c: Coincident(g3,g-5)
    c: Coincident(g3,g4)
    c: Horizontal(g4)
    c: Coincident(g4,g5)
    c: Coincident(g5,g6)
    c: Coincident(g6,g3)
    c: Horizontal(g6)
    c: Parallel(g-4,g5)
    c: Distance(g5,g-4) = 0.1
FEATURE [PartDesign::Pocket] Pocket016
  BaseFeature = -> Pad019
  Direction = (0,-1,2e-16)
  Length = 5
  Length2 = 5
  Midplane = true
  Profile = -> Sketch047
  ReferenceAxis = -> Sketch047 [N_Axis]
  Refine = true
  Suppressed = false
  Type = 1
FEATURE [PartDesign::SubShapeBinder] Binder023
  BindCopyOnChange = 0
  BindMode = 0
  ClaimChildren = false
  Context = -> Body009 [Binder023.]
  Fuse = false
  MakeFace = true
  OffsetFill = false
  OffsetIntersection = false
  OffsetJoinType = 0
  OffsetOpenResult = false
  PartialLoad = false
  Refine = true
  Relative = true
  Support = -> [Body006[Sketch043.]]
  _Version = 2
FEATURE [Sketcher::SketchObject] Sketch048
  ArcFitTolerance = 1e-06
  AttachmentSupport = -> [Pocket016]
  ExternalGeometry = -> [Binder023]
  FullyConstrained = true
  MakeInternals = false
  MapMode = 5
  Placement = pos=(0,0,4) rot=(0,0,1;0rad)
  sketch-geometry (1):
    g0: Circle CenterX=62.8197 CenterY=0 CenterZ=0 NormalX=0 NormalY=0 NormalZ=1 AngleXU=0 Radius=1.5
  constraints (2):
    c: Coincident(g0,g-3)
    c: Equal(g0,g-3)
FEATURE [PartDesign::Hole] Hole009
  BaseFeature = -> Pocket016
  CustomThreadClearance = 0
  Depth = 141.896
  DepthType = 1
  Diameter = 2.4
  DrillForDepth = false
  DrillPoint = 1
  DrillPointAngle = 118
  HoleCutCountersinkAngle = 90
  HoleCutCustomValues = false
  HoleCutDepth = 1
  HoleCutDiameter = 4
  HoleCutType = 1
  ModelThread = false
  Profile = -> Sketch048
  Refine = true
  Suppressed = false
  Tapered = false
  TaperedAngle = 90
  ThreadClass = 0
  ThreadDepth = 141.896
  ThreadDepthType = 0
  ThreadDirection = 0
  ThreadFit = 0
  ThreadSize = 6
  ThreadType = 1
  Threaded = false
  UseCustomThreadClearance = false
FEATURE [PartDesign::Body] Body009  label="ElectronicsLid"
  AllowCompound = false
  Group = -> [Binder018,Binder019,Sketch046,Pad018,Binder020,Pad019,Sketch047,Pocket016,Sketch048,Hole009,Binder022,Binder023]
  Origin = -> Origin010
  Tip = -> Hole009
COMPONENT P5 — recipe-attached ("Foot001", modeled in this document).
Construction recipe (the document's own serialized feature program — sketch geometry with constraints, then the solid features built on it; lengths are millimeters unless a unit is written):

FEATURE [PartDesign::SubShapeBinder] Binder001
  BindCopyOnChange = 0
  BindMode = 0
  ClaimChildren = false
  Context = -> Body002 [Binder001.]
  Fuse = false
  MakeFace = true
  OffsetFill = false
  OffsetIntersection = false
  OffsetJoinType = 0
  OffsetOpenResult = false
  PartialLoad = false
  Refine = true
  Relative = true
  Support = -> [Body[Sketch.]]
  _Version = 2
FEATURE [PartDesign::SubShapeBinder] Binder002
  BindCopyOnChange = 0
  BindMode = 0
  ClaimChildren = false
  Context = -> Body002 [Binder002.]
  Fuse = false
  MakeFace = true
  OffsetFill = false
  OffsetIntersection = false
  OffsetJoinType = 0
  OffsetOpenResult = false
  PartialLoad = false
  Refine = true
  Relative = true
  Support = -> [Body001[Sketch001.]]
  _Version = 2
FEATURE [Sketcher::SketchObject] Sketch006  label="FootProfile"
  ArcFitTolerance = 1e-06
  AttachmentSupport = -> [XZ_Plane002]
  ExternalGeometry = -> [Binder001,Binder002]
  FullyConstrained = true
  MakeInternals = false
  MapMode = 5
  Placement = pos=(0,0,0) rot=(1,0,0;1.5708rad)
  sketch-geometry (12):
    g0: LineSegment StartX=-9.7 StartY=-4 StartZ=0 EndX=-9.7 EndY=-11 EndZ=0
    g1: LineSegment StartX=-6.1 StartY=-4 StartZ=0 EndX=-6.1 EndY=-2.6 EndZ=0
    g2: LineSegment StartX=-6.7 StartY=-2 StartZ=0 EndX=-7.7 EndY=-2 EndZ=0
    g3: LineSegment StartX=-6.1 StartY=-4 StartZ=0 EndX=0 EndY=-4 EndZ=0
    g4: LineSegment StartX=0 StartY=-4 StartZ=0 EndX=0 EndY=-11 EndZ=0
    g5: LineSegment StartX=0 StartY=-11 StartZ=0 EndX=-9.7 EndY=-11 EndZ=0
    g6: ArcOfCircle [constr] CenterX=-6.7 CenterY=-2.6 CenterZ=0 NormalX=0 NormalY=0 NormalZ=1 AngleXU=0 Radius=0.6 StartAngle=1e-16 EndAngle=1.5708
    g7: GeomPoint [constr] X=-6.1 Y=-2 Z=0
    g8: LineSegment StartX=-6.1 StartY=-2.6 StartZ=0 EndX=-6.7 EndY=-2 EndZ=0
    g9: ArcOfCircle [constr] CenterX=-7.7 CenterY=-4 CenterZ=0 NormalX=0 NormalY=0 NormalZ=1 AngleXU=0 Radius=2 StartAngle=1.5708 EndAngle=3.14159
    g10: GeomPoint [constr] X=-9.7 Y=-2 Z=0
    g11: LineSegment StartX=-7.7 StartY=-2 StartZ=0 EndX=-9.7 EndY=-4 EndZ=0
  constraints (30):
    c: Vertical(g0)
    c: Vertical(g1)
    c: Horizontal(g2)
    c: Distance(g-3,g1) = 0.1
    c: Distance(g-4,g2) = 1
    c: Coincident(g3,g1)
    c: PointOnObject(g3,g-2)
    c: Horizontal(g3)
    c: Coincident(g4,g3)
    c: Vertical(g4)
    c: Coincident(g5,g4)
    c: Coincident(g5,g0)
    c: Horizontal(g5)
    c: Distance(g4,g4) = 7  'BaseThickness'
    c: PointOnObject(g1,g-5)
    c: PointOnObject(g7,g2)
    c: PointOnObject(g7,g1)
    c: Tangent(g2,g6) = -1.5708
    c: Tangent(g1,g6) = -1.5708
    c: Coincident(g8,g2)
    c: Coincident(g8,g1)
    c: PointOnObject(g10,g2)
    c: PointOnObject(g10,g0)
    c: Tangent(g2,g9) = -1.5708
    c: Tangent(g0,g9) = -1.5708
    c: Coincident(g11,g2)
    c: Coincident(g11,g0)
    c: Distance(g1,g7) = 0.6
    c: Distance(g2,g2) = 1
    c: Horizontal(g9,g1)
FEATURE [PartDesign::Pad] Pad003
  Direction = (0,-1,2e-16)
  Length = 20
  Length2 = 5
  Midplane = true
  Placement = pos=(0,0,0) rot=(1,0,0;1.5708rad)
  Profile = -> Sketch006
  ReferenceAxis = -> Sketch006 [N_Axis]
  Refine = true
  Suppressed = false
  Type = 4
FEATURE [PartDesign::Mirrored] Mirrored
  BaseFeature = -> Pad003
  MirrorPlane = -> Sketch006 [V_Axis]
  Originals = -> [Pad003]
  Placement = pos=(0,0,0) rot=(1,0,0;1.5708rad)
  Refine = true
  Suppressed = false
  TransformMode = 0
FEATURE [Sketcher::SketchObject] Sketch007
  ArcFitTolerance = 1e-06
  AttachmentSupport = -> [Mirrored]
  FullyConstrained = false
  MakeInternals = false
  MapMode = 5
  Placement = pos=(0,-1.8e-15,-4) rot=(0,0,1;3.14159rad)
  sketch-geometry (1):
    g0: Circle CenterX=0 CenterY=0 CenterZ=0 NormalX=0 NormalY=0 NormalZ=1 AngleXU=0 Radius=1.1986
  constraints (1):
    c: Coincident(g0,g-1)
FEATURE [PartDesign::Hole] Hole002  label="FootHole"
  BaseFeature = -> Mirrored
  CustomThreadClearance = 0
  Depth = 109.851
  DepthType = 1
  Diameter = 4.4
  DrillForDepth = false
  DrillPoint = 1
  DrillPointAngle = 118
  HoleCutCountersinkAngle = 90
  HoleCutCustomValues = false
  HoleCutDepth = 0
  HoleCutDiameter = 6.1
  HoleCutType = 0
  ModelThread = false
  Placement = pos=(0,0,0) rot=(1,0,0;1.5708rad)
  Profile = -> Sketch007
  Refine = true
  Suppressed = false
  Tapered = false
  TaperedAngle = 90
  ThreadClass = 0
  ThreadDepth = 109.851
  ThreadDepthType = 0
  ThreadDirection = 0
  ThreadFit = 0
  ThreadSize = 0
  ThreadType = 0
  Threaded = false
  UseCustomThreadClearance = false
FEATURE [Sketcher::SketchObject] Sketch028  label="FootPads"
  ArcFitTolerance = 1e-06
  AttachmentSupport = -> [Hole002]
  ExternalGeometry = -> [Hole002]
  FullyConstrained = true
  MakeInternals = false
  MapMode = 5
  Placement = pos=(0,-4.7e-15,-11) rot=(1,0,0;3.14159rad)
  sketch-geometry (3):
    g0: Circle CenterX=0 CenterY=12 CenterZ=0 NormalX=0 NormalY=0 NormalZ=1 AngleXU=0 Radius=5
    g1: GeomPoint X=0 Y=20 Z=0
    g2: GeomPoint X=0 Y=17 Z=0
  constraints (7):
    c: PointOnObject(g0,g-2)
    c: Diameter(g0) = 10  'FootDiameter'
    c: PointOnObject(g1,g-2)
    c: PointOnObject(g2,g0)
    c: PointOnObject(g2,g-2)
    c: Distance(g2,g1) = 3
    c: PointOnObject(g1,g-3)
FEATURE [PartDesign::Pocket] Pocket008  label="FootPadPocket"
  BaseFeature = -> Hole002
  Direction = (0,0,1)
  Length = 3
  Length2 = 5
  Placement = pos=(0,0,0) rot=(1,0,0;1.5708rad)
  Profile = -> Sketch028
  ReferenceAxis = -> Sketch028 [N_Axis]
  Refine = true
  Suppressed = false
  Type = 0
FEATURE [Sketcher::SketchObject] Sketch032  label="FootEndBlock"
  ArcFitTolerance = 1e-06
  AttachmentSupport = -> [Pocket008]
  ExternalGeometry = -> [Pocket008]
  FullyConstrained = true
  MakeInternals = false
  MapMode = 5
  Placement = pos=(0,-1.8e-15,-4) rot=(0,0,1;3.14159rad)
  expr: Constraints[11] = <<RailHolePosition>>.Constraints.E + 1 mm
  sketch-geometry (5):
    g0: LineSegment StartX=-9.7 StartY=20 StartZ=0 EndX=-9.7 EndY=8.5 EndZ=0
    g1: LineSegment StartX=-9.7 StartY=8.5 StartZ=0 EndX=9.7 EndY=8.5 EndZ=0
    g2: LineSegment StartX=9.7 StartY=8.5 StartZ=0 EndX=9.7 EndY=20 EndZ=0
    g3: LineSegment StartX=9.7 StartY=20 StartZ=0 EndX=-9.7 EndY=20 EndZ=0
    g4: LineSegment [constr] StartX=-9.7 StartY=13.5 StartZ=0 EndX=9.7 EndY=13.5 EndZ=0
  constraints (15):
    c: Coincident(g0,g1)
    c: Coincident(g1,g2)
    c: Coincident(g2,g3)
    c: Coincident(g3,g0)
    c: Vertical(g0)
    c: Vertical(g2)
    c: Horizontal(g1)
    c: Horizontal(g3)
    c: PointOnObject(g4,g0)
    c: PointOnObject(g4,g2)
    c: Horizontal(g4)
    c: DistanceY(g-1,g4) = 13.5
    c: DistanceY(g1,g4) = 5  'Overhang'
    c: Vertical(g0,g-3)
    c: Coincident(g-3,g2)
FEATURE [PartDesign::Pad] Pad013
  BaseFeature = -> Pocket008
  Direction = (0,0,1)
  Length = 13
  Length2 = 10
  Placement = pos=(0,0,0) rot=(1,0,0;1.5708rad)
  Profile = -> Sketch032
  ReferenceAxis = -> Sketch032 [N_Axis]
  Refine = true
  Suppressed = false
  Type = 0
  expr: Length = <<Block Cross-Section>>.Constraints.Height
FEATURE [Sketcher::SketchObject] Sketch033
  ArcFitTolerance = 1e-06
  AttachmentSupport = -> [Pad013]
  FullyConstrained = true
  MakeInternals = false
  MapMode = 5
  Placement = pos=(0,-8.5,1.9e-15) rot=(-1,0,0;1.5708rad)
  expr: Constraints[10] = <<Rail Cross-Section>>.Constraints.Hr + 0.5 mm
  sketch-geometry (4):
    g0: LineSegment StartX=-6.1 StartY=4 StartZ=0 EndX=-6.1 EndY=-4.5 EndZ=0
    g1: LineSegment StartX=-6.1 StartY=-4.5 StartZ=0 EndX=6.1 EndY=-4.5 EndZ=0
    g2: LineSegment StartX=6.1 StartY=-4.5 StartZ=0 EndX=6.1 EndY=4 EndZ=0
    g3: LineSegment StartX=6.1 StartY=4 StartZ=0 EndX=-6.1 EndY=4 EndZ=0
  constraints (11):
    c: Coincident(g0,g1)
    c: Coincident(g1,g2)
    c: Coincident(g2,g3)
    c: Coincident(g3,g0)
    c: Vertical(g0)
    c: Vertical(g2)
    c: Horizontal(g1)
    c: Horizontal(g3)
    c: Coincident(g0,g-3)
    c: PointOnObject(g-4,g2)
    c: DistanceY(g2,g2) = 8.5
FEATURE [PartDesign::Pocket] Pocket010
  BaseFeature = -> Pad013
  Direction = (0,-1,-2e-16)
  Length = 5
  Length2 = 5
  Placement = pos=(0,0,0) rot=(1,0,0;1.5708rad)
  Profile = -> Sketch033
  ReferenceAxis = -> Sketch033 [N_Axis]
  Refine = true
  Suppressed = false
  Type = 0
  expr: Length = <<FootEndBlock>>.Constraints.Overhang
FEATURE [PartDesign::Fillet] Fillet004
  Base = -> Pocket010 [Edge24,Edge50,Edge33,Edge25,Edge32]
  BaseFeature = -> Pocket010
  Placement = pos=(0,0,0) rot=(1,0,0;1.5708rad)
  Radius = 5
  Refine = true
  SupportTransform = false
  Suppressed = false
  UseAllEdges = false
FEATURE [PartDesign::Body] Body002  label="Foot"
  AllowCompound = false
  Group = -> [Binder001,Binder002,Sketch006,Pad003,Mirrored,Sketch007,Hole002,Sketch028,Pocket008,Sketch032,Pad013,Sketch033,Pocket010,Fillet004]
  Origin = -> Origin002
  Tip = -> Fillet004
COMPONENT P6 — same part as P5; its construction recipe is shown at P5.
COMPONENT P7 — recipe-attached ("PicoW001", modeled in this document).
Construction recipe (the document's own serialized feature program — sketch geometry with constraints, then the solid features built on it; lengths are millimeters unless a unit is written):

FEATURE [Sketcher::SketchObject] Sketch034
  ArcFitTolerance = 1e-06
  AttachmentSupport = -> [XY_Plane009]
  FullyConstrained = true
  MakeInternals = false
  MapMode = 5
  sketch-geometry (14):
    g0: LineSegment StartX=-10.5 StartY=-25.5 StartZ=0 EndX=10.5 EndY=-25.5 EndZ=0
    g1: LineSegment StartX=10.5 StartY=-25.5 StartZ=0 EndX=10.5 EndY=25.5 EndZ=0
    g2: LineSegment StartX=10.5 StartY=25.5 StartZ=0 EndX=-10.5 EndY=25.5 EndZ=0
    g3: LineSegment StartX=-10.5 StartY=25.5 StartZ=0 EndX=-10.5 EndY=-25.5 EndZ=0
    g4: GeomPoint [constr] X=0 Y=0 Z=0
    g5: LineSegment [constr] StartX=-5.7 StartY=-23.5 StartZ=0 EndX=5.7 EndY=-23.5 EndZ=0
    g6: LineSegment [constr] StartX=5.7 StartY=-23.5 StartZ=0 EndX=5.7 EndY=23.5 EndZ=0
    g7: LineSegment [constr] StartX=5.7 StartY=23.5 StartZ=0 EndX=-5.7 EndY=23.5 EndZ=0
    g8: LineSegment [constr] StartX=-5.7 StartY=23.5 StartZ=0 EndX=-5.7 EndY=-23.5 EndZ=0
    g9: GeomPoint [constr] X=0 Y=0 Z=0
    g10: Circle CenterX=-5.7 CenterY=23.5 CenterZ=0 NormalX=0 NormalY=0 NormalZ=1 AngleXU=0 Radius=1.05
    g11: Circle CenterX=5.7 CenterY=23.5 CenterZ=0 NormalX=0 NormalY=0 NormalZ=1 AngleXU=0 Radius=1.05
    g12: Circle CenterX=-5.7 CenterY=-23.5 CenterZ=0 NormalX=0 NormalY=0 NormalZ=1 AngleXU=0 Radius=1.05
    g13: Circle CenterX=5.7 CenterY=-23.5 CenterZ=0 NormalX=0 NormalY=0 NormalZ=1 AngleXU=0 Radius=1.05
  constraints (32):
    c: Coincident(g0,g1)
    c: Coincident(g1,g2)
    c: Coincident(g2,g3)
    c: Coincident(g3,g0)
    c: Horizontal(g0)
    c: Horizontal(g2)
    c: Vertical(g1)
    c: Vertical(g3)
    c: Symmetric(g2,g0,g4)
    c: Distance(g1,g3) = 21
    c: Distance(g0,g2) = 51  'Height'
    c: Coincident(g4,g-1)
    c: Coincident(g5,g6)
    c: Coincident(g6,g7)
    c: Coincident(g7,g8)
    c: Coincident(g8,g5)
    c: Horizontal(g5)
    c: Horizontal(g7)
    c: Vertical(g6)
    c: Vertical(g8)
    c: Symmetric(g7,g5,g9)
    c: Distance(g6,g8) = 11.4
    c: Coincident(g9,g4)
    c: Distance(g5,g0) = 2
    c: Coincident(g10,g7)
    c: Coincident(g11,g6)
    c: Coincident(g12,g5)
    c: Coincident(g13,g5)
    c: Equal(g10,g11)
    c: Equal(g11,g12)
    c: Equal(g12,g13)
    c: Diameter(g10) = 2.1  'HoleDiameter'
FEATURE [PartDesign::Pad] Pad014  label="Board"
  Direction = (0,0,1)
  Length = 1
  Length2 = 10
  Profile = -> Sketch034
  ReferenceAxis = -> Sketch034 [N_Axis]
  Refine = true
  Suppressed = false
  Type = 0
FEATURE [Sketcher::SketchObject] Sketch035
  ArcFitTolerance = 1e-06
  AttachmentOffset = pos=(0,0,-0.3) rot=(0,0,1;0rad)
  AttachmentSupport = -> [Pad014]
  ExternalGeometry = -> [Pad014]
  FullyConstrained = true
  MakeInternals = false
  MapMode = 5
  Placement = pos=(0,0,0.7) rot=(0,0,1;0rad)
  sketch-geometry (5):
    g0: LineSegment StartX=-4 StartY=26.8 StartZ=0 EndX=-4 EndY=20.8 EndZ=0
    g1: LineSegment StartX=-4 StartY=20.8 StartZ=0 EndX=4 EndY=20.8 EndZ=0
    g2: LineSegment StartX=4 StartY=20.8 StartZ=0 EndX=4 EndY=26.8 EndZ=0
    g3: LineSegment StartX=4 StartY=26.8 StartZ=0 EndX=-4 EndY=26.8 EndZ=0
    g4: GeomPoint X=0 Y=26.8 Z=0
  constraints (13):
    c: Coincident(g0,g1)
    c: Coincident(g1,g2)
    c: Coincident(g2,g3)
    c: Coincident(g3,g0)
    c: Vertical(g0)
    c: Vertical(g2)
    c: Horizontal(g1)
    c: Horizontal(g3)
    c: Distance(g0,g2) = 8
    c: DistanceY(g0,g0) = 6
    c: Distance(g-3,g3) = 1.3
    c: Symmetric(g3,g3,g4)
    c: PointOnObject(g4,g-2)
FEATURE [PartDesign::Pad] Pad015  label="Socket"
  BaseFeature = -> Pad014
  Direction = (0,0,1)
  Length = 3
  Length2 = 10
  Profile = -> Sketch035
  ReferenceAxis = -> Sketch035 [N_Axis]
  Refine = true
  Suppressed = false
  Type = 0
FEATURE [Sketcher::SketchObject] Sketch036
  ArcFitTolerance = 1e-06
  AttachmentSupport = -> [Pad015]
  ExternalGeometry = -> [Pad015]
  FullyConstrained = true
  MakeInternals = false
  MapMode = 5
  Placement = pos=(0,26.8,0) rot=(0,0.707107,0.707107;3.14159rad)
  sketch-geometry (5):
    g0: LineSegment StartX=-5.5 StartY=-2.3 StartZ=0 EndX=5.5 EndY=-2.3 EndZ=0
    g1: LineSegment StartX=5.5 StartY=-2.3 StartZ=0 EndX=5.5 EndY=6.7 EndZ=0
    g2: LineSegment StartX=5.5 StartY=6.7 StartZ=0 EndX=-5.5 EndY=6.7 EndZ=0
    g3: LineSegment StartX=-5.5 StartY=6.7 StartZ=0 EndX=-5.5 EndY=-2.3 EndZ=0
    g4: GeomPoint [constr] X=1e-16 Y=2.2 Z=0
  constraints (12):
    c: Coincident(g0,g1)
    c: Coincident(g1,g2)
    c: Coincident(g2,g3)
    c: Coincident(g3,g0)
    c: Horizontal(g0)
    c: Horizontal(g2)
    c: Vertical(g1)
    c: Vertical(g3)
    c: Symmetric(g2,g0,g4)
    c: Distance(g1,g3) = 11
    c: Distance(g0,g2) = 9
    c: Symmetric(g-3,g-4,g4)
FEATURE [PartDesign::Pad] Pad016  label="Keepout"
  BaseFeature = -> Pad015
  Direction = (0,1,-2e-16)
  Length = 10
  Length2 = 10
  Profile = -> Sketch036
  ReferenceAxis = -> Sketch036 [N_Axis]
  Refine = true
  Suppressed = false
  Type = 0
FEATURE [PartDesign::Body] Body008  label="PicoW"
  AllowCompound = false
  Group = -> [Sketch034,Pad014,Sketch035,Pad015,Sketch036,Pad016]
  Origin = -> Origin009
  Placement = pos=(90,0,-6) rot=(0,0,1;3.14159rad)
  Tip = -> Pad016
COMPONENT P8 — recipe-attached ("Pinion001", modeled in this document).
Construction recipe (the document's own serialized feature program — sketch geometry with constraints, then the solid features built on it; lengths are millimeters unless a unit is written):

FEATURE [PartDesign::SubShapeBinder] Binder010
  BindCopyOnChange = 0
  BindMode = 0
  ClaimChildren = false
  Context = -> Body005 [Binder010.]
  Fuse = false
  MakeFace = true
  OffsetFill = false
  OffsetIntersection = false
  OffsetJoinType = 0
  OffsetOpenResult = false
  PartialLoad = false
  Refine = true
  Relative = true
  Support = -> [Body004[Sketch012.]]
  _Version = 2
FEATURE [PartDesign::SubShapeBinder] Binder011
  BindCopyOnChange = 0
  BindMode = 0
  ClaimChildren = false
  Context = -> Body005 [Binder011.]
  Fuse = false
  MakeFace = true
  OffsetFill = false
  OffsetIntersection = false
  OffsetJoinType = 0
  OffsetOpenResult = false
  PartialLoad = false
  Refine = true
  Relative = true
  Support = -> [Body002[Sketch006.]]
  _Version = 2
FEATURE [Sketcher::SketchObject] Sketch019  label="PinionCrossSection"
  ArcFitTolerance = 1e-06
  AttachmentSupport = -> [XZ_Plane005]
  ExternalGeometry = -> [Binder010,Binder011]
  FullyConstrained = true
  MakeInternals = false
  MapMode = 5
  Placement = pos=(0,0,0) rot=(1,0,0;1.5708rad)
  expr: Constraints[46] = <<RackStringEnds>>.Constraints.Length / pi
  sketch-geometry (27):
    g0: LineSegment StartX=14.9142 StartY=17 StartZ=0 EndX=18.9142 EndY=13 EndZ=0
    g1: LineSegment StartX=18.9142 StartY=13 StartZ=0 EndX=15.2909 EndY=9.37671 EndZ=0
    g2: LineSegment StartX=15.7474 StartY=8.53387 StartZ=0 EndX=113.128 EndY=29.0174 EndZ=0
    g3: LineSegment StartX=113.128 StartY=29.0174 StartZ=0 EndX=112.51 EndY=31.9532 EndZ=0
    g4: LineSegment StartX=112.51 StartY=31.9532 StartZ=0 EndX=23.9043 EndY=13.3153 EndZ=0
    g5: ArcOfCircle CenterX=16.794 CenterY=11.8197 CenterZ=0 NormalX=0 NormalY=0 NormalZ=1 AngleXU=0 Radius=7.26587 StartAngle=0.207323 EndAngle=1.64585
    g6: LineSegment StartX=14.9849 StartY=18.4849 StartZ=0 EndX=14.9142 EndY=18.4142 EndZ=0
    g7: LineSegment [constr] StartX=13.5 StartY=17 StartZ=0 EndX=17.5 EndY=13 EndZ=0
    g8: LineSegment [constr] StartX=17.5 StartY=13 StartZ=0 EndX=13.5 EndY=9 EndZ=0
    g9: ArcOfCircle [constr] CenterX=13.5 CenterY=9 CenterZ=0 NormalX=0 NormalY=0 NormalZ=-1 AngleXU=2.35619 Radius=1 StartAngle=1.5708 EndAngle=4.71239
    g10: LineSegment [constr] StartX=16.0858 StartY=13 StartZ=0 EndX=12.7929 EndY=9.70711 EndZ=0
    g11: LineSegment [constr] StartX=12.7929 StartY=16.2929 StartZ=0 EndX=16.0858 EndY=13 EndZ=0
    g12: ArcOfCircle [constr] CenterX=13.5 CenterY=17 CenterZ=0 NormalX=0 NormalY=0 NormalZ=-1 AngleXU=-2.35619 Radius=1 StartAngle=1.5708 EndAngle=4.71239
    g13: LineSegment [constr] StartX=14.2071 StartY=17.7071 StartZ=0 EndX=18.2071 EndY=13.7071 EndZ=0
    g14: ArcOfCircle [constr] CenterX=17.5 CenterY=13 CenterZ=0 NormalX=0 NormalY=0 NormalZ=-1 AngleXU=0.785398 Radius=1 StartAngle=1.5708 EndAngle=3.14159
    g15: LineSegment [constr] StartX=18.2071 StartY=12.2929 StartZ=0 EndX=14.2071 EndY=8.29289 EndZ=0
    g16: ArcOfCircle CenterX=16.3991 CenterY=17.0707 CenterZ=0 NormalX=0 NormalY=0 NormalZ=1 AngleXU=0 Radius=2 StartAngle=1.64585 EndAngle=2.35619
    g17: ArcOfCircle CenterX=15.6213 CenterY=17.7071 CenterZ=0 NormalX=0 NormalY=0 NormalZ=1 AngleXU=0 Radius=1 StartAngle=2.35619 EndAngle=3.92699
    g18: GeomPoint [constr] X=14.2071 Y=17.7071 Z=0
    g19: ArcOfCircle CenterX=15.6445 CenterY=9.02316 CenterZ=0 NormalX=0 NormalY=0 NormalZ=1 AngleXU=0 Radius=0.5 StartAngle=2.35619 EndAngle=4.91971
    g20: GeomPoint [constr] X=14.102 Y=8.18776 Z=0
    g21: LineSegment [constr] StartX=104.732 StartY=25.2077 StartZ=0 EndX=122.347 EndY=28.9128 EndZ=0
    g22: LineSegment [constr] StartX=122.347 StartY=28.9128 StartZ=0 EndX=129.963 EndY=-7.29486 EndZ=0
    g23: LineSegment [constr] StartX=129.963 StartY=-7.29486 StartZ=0 EndX=112.348 EndY=-11 EndZ=0
    g24: LineSegment [constr] StartX=112.348 StartY=-11 StartZ=0 EndX=104.732 EndY=25.2077 EndZ=0
    g25: GeomPoint [constr] X=113.539 Y=27.0602 Z=0
    g26: LineSegment [constr] StartX=13.5 StartY=9 StartZ=0 EndX=15.2909 EndY=9.37671 EndZ=0
  constraints (66):
    c: Coincident(g0,g1)
    c: Coincident(g2,g3)
    c: Coincident(g3,g4)
    c: Perpendicular(g4,g5) = 4.71239
    c: Parallel(g2,g4)
    c: Perpendicular(g2,g3)
    c: Coincident(g-3,g7)
    c: Coincident(g7,g8)
    c: Coincident(g8,g-4)
    c: PointOnObject(g-4,g8)
    c: PointOnObject(g-3,g7)
    c: Tangent(g9,g10) = -1.5708
    c: Tangent(g9,g15) = 1.5708
    c: Coincident(g10,g11)
    c: Tangent(g11,g12) = -1.5708
    c: Tangent(g12,g13) = 1.5708
    c: Tangent(g13,g14) = 1.5708
    c: Tangent(g14,g15) = 1.5708
    c: Parallel(g15,g8)
    c: Coincident(g9,g8)
    c: Parallel(g10,g8)
    c: Parallel(g11,g7)
    c: Coincident(g12,g7)
    c: Parallel(g13,g7)
    c: Coincident(g14,g7)
    c: Distance(g14,g14) = 1
    c: PointOnObject(g18,g13)
    c: PointOnObject(g0,g13)
    c: PointOnObject(g20,g15)
    c: PointOnObject(g0,g15)
    c: PointOnObject(g12,g6)
    c: Perpendicular(g6,g0)
    c: Distance(g3,g3) = 3  'thickness'
    c: Tangent(g5,g16) = -1.5708
    c: Tangent(g6,g16) = -1.5708
    c: PointOnObject(g18,g0)
    c: PointOnObject(g18,g6)
    c: Tangent(g0,g17) = -1.5708
    c: Tangent(g6,g17) = -1.5708
    c: PointOnObject(g20,g1)
    c: PointOnObject(g20,g2)
    c: Tangent(g1,g19) = -1.5708
    c: Tangent(g2,g19) = -1.5708
    c: Radius(g19) = 0.5
    c: Radius(g17) = 1
    c: Radius(g16) = 2
    c: Distance(g0,g3) = 95.493
    c: Coincident(g21,g22)
    c: Coincident(g22,g23)
    c: Coincident(g23,g24)
    c: Coincident(g24,g21)
    c: Perpendicular(g21,g24)
    c: Perpendicular(g22,g23)
    c: Perpendicular(g22,g21)
    c: Distance(g22,g22) = 37  'ServoBodyHeight'
    c: Distance(g23,g23) = 18  'ServoBodyWidth'
    c: Symmetric(g21,g21,g25)
    c: Parallel(g2,g21)
    c: PointOnObject(g25,g3)
    c: Distance(g0,g4) = 5
    c: Distance(g6,g6) = 0.1
    c: Horizontal(g-5,g23)
    c: Distance(g3,g25) = 5  'ServoShaftLength'
    c: Coincident(g26,g8)
    c: Parallel(g26,g2)
    c: Coincident(g26,g1)
FEATURE [PartDesign::Revolution] Revolution
  Angle = 190
  Angle2 = 60
  Axis = (-0.205841,2e-16,0.978585)
  Base = (113.128,6.4e-15,29.0174)
  Midplane = true
  Placement = pos=(0,0,0) rot=(1,0,0;1.5708rad)
  Profile = -> Sketch019
  ReferenceAxis = -> Sketch019 [Edge5]
  Refine = true
  Reversed = true
  Suppressed = false
  Type = 0
FEATURE [Sketcher::SketchObject] Sketch020
  ArcFitTolerance = 1e-06
  AttachmentSupport = -> [XZ_Plane005]
  ExternalGeometry = -> [Revolution]
  FullyConstrained = true
  MakeInternals = false
  MapMode = 5
  Placement = pos=(0,0,0) rot=(1,0,0;1.5708rad)
  expr: Constraints[0] = <<RackStringEnds>>.Constraints.stringHoleDiameter
  sketch-geometry (2):
    g0: Circle CenterX=112.356 CenterY=32.6871 CenterZ=0 NormalX=0 NormalY=0 NormalZ=1 AngleXU=0 Radius=0.75
    g1: GeomPoint [constr] X=112.51 Y=31.9532 Z=0
  constraints (4):
    c: Diameter(g0) = 1.5
    c: PointOnObject(g0,g-3)
    c: PointOnObject(g1,g0)
    c: Coincident(g1,g-5)
FEATURE [PartDesign::Pocket] Pocket004
  BaseFeature = -> Revolution
  Direction = (0,1,-2e-16)
  Length = 5
  Length2 = 5
  Midplane = true
  Placement = pos=(0,0,0) rot=(1,0,0;1.5708rad)
  Profile = -> Sketch020
  ReferenceAxis = -> Sketch020 [N_Axis]
  Refine = true
  Suppressed = false
  Type = 1
FEATURE [Sketcher::SketchObject] Sketch021
  ArcFitTolerance = 1e-06
  AttachmentSupport = -> [Pocket004]
  ExternalGeometry = -> [Pocket004]
  FullyConstrained = true
  MakeInternals = false
  MapMode = 5
  Placement = pos=(-1.05178,2.2e-15,5.00023) rot=(0.994632,0,0.103476;3.14159rad)
  sketch-geometry (5):
    g0: Ellipse CenterX=116.678 CenterY=-1.42e-14 CenterZ=0 NormalX=0 NormalY=0 NormalZ=1 MajorRadius=21 MinorRadius=10 AngleXU=-1.5708
    g1: LineSegment [constr] StartX=116.678 StartY=-21 StartZ=0 EndX=116.678 EndY=21 EndZ=0
    g2: LineSegment [constr] StartX=126.678 StartY=-3.26795e-06 StartZ=0 EndX=106.678 EndY=3.26795e-06 EndZ=0
    g3: GeomPoint [constr] X=116.678 Y=-18.4662 Z=0
    g4: GeomPoint [constr] X=116.678 Y=18.4662 Z=0
  constraints (5):
    c: InternalAlignment(g1-g4 -> g0) x4
    c: Distance(g0,g1) = 21
    c: Angle(g1) = 1.5708
    c: Distance(g0,g2) = 10
    c: Coincident(g0,g-3)
FEATURE [PartDesign::Pad] Pad007
  BaseFeature = -> Pocket004
  Direction = (0.205841,0,-0.978585)
  Length = 3
  Length2 = 10
  Placement = pos=(0,0,0) rot=(1,0,0;1.5708rad)
  Profile = -> Sketch021
  ReferenceAxis = -> Sketch021 [N_Axis]
  Refine = true
  Reversed = true
  Suppressed = false
  Type = 0
  expr: Length = <<PinionCrossSection>>.Constraints.thickness
FEATURE [Sketcher::SketchObject] Sketch022  label="PinionServoMountingHoles"
  ArcFitTolerance = 1e-06
  AttachmentSupport = -> [Pad007]
  ExternalGeometry = -> [Pad007]
  FullyConstrained = true
  MakeInternals = false
  MapMode = 5
  Placement = pos=(-1.6693,3.5e-15,7.93599) rot=(-0.103476,0,0.994632;3.14159rad)
  sketch-geometry (4):
    g0: Circle CenterX=-116.678 CenterY=-1.26e-14 CenterZ=0 NormalX=0 NormalY=0 NormalZ=1 AngleXU=0 Radius=4
    g1: Circle CenterX=-116.678 CenterY=17 CenterZ=0 NormalX=0 NormalY=0 NormalZ=1 AngleXU=0 Radius=0.75
    g2: Circle CenterX=-101.678 CenterY=0 CenterZ=0 NormalX=0 NormalY=0 NormalZ=1 AngleXU=0 Radius=0.75
    g3: Circle CenterX=-116.678 CenterY=-17 CenterZ=0 NormalX=0 NormalY=0 NormalZ=1 AngleXU=0 Radius=0.75
  constraints (10):
    c: Diameter(g0) = 8  'ServoShaftDiameter'
    c: PointOnObject(g2,g-1)
    c: Equal(g2,g1)
    c: Equal(g1,g3)
    c: Diameter(g1) = 1.5
    c: DistanceX(g0,g2) = 15
    c: Symmetric(g1,g3,g0)
    c: DistanceY(g3,g1) = 34
    c: Vertical(g1,g3)
    c: Coincident(g0,g-3)
FEATURE [PartDesign::Pocket] Pocket005
  BaseFeature = -> Pad007
  Direction = (0.205841,0,-0.978585)
  Length = 5
  Length2 = 5
  Placement = pos=(0,0,0) rot=(1,0,0;1.5708rad)
  Profile = -> Sketch022
  ReferenceAxis = -> Sketch022 [N_Axis]
  Refine = true
  Suppressed = false
  Type = 1
FEATURE [PartDesign::Body] Body005  label="Pinion"
  AllowCompound = false
  Group = -> [Binder010,Binder011,Sketch019,Revolution,Sketch020,Pocket004,Sketch021,Pad007,Sketch022,Pocket005]
  Origin = -> Origin005
  Tip = -> Pocket005
COMPONENT P9 — recipe-attached ("Rack001", modeled in this document).
Construction recipe (the document's own serialized feature program — sketch geometry with constraints, then the solid features built on it; lengths are millimeters unless a unit is written):

FEATURE [PartDesign::SubShapeBinder] Binder008
  BindCopyOnChange = 0
  BindMode = 0
  ClaimChildren = false
  Context = -> Body004 [Binder008.]
  Fuse = false
  MakeFace = true
  OffsetFill = false
  OffsetIntersection = false
  OffsetJoinType = 0
  OffsetOpenResult = false
  PartialLoad = false
  Refine = true
  Relative = true
  Support = -> [Body001[Sketch001.]]
  _Version = 2
FEATURE [Sketcher::SketchObject] Sketch012  label="RackProfile"
  ArcFitTolerance = 1e-06
  AttachmentSupport = -> [XZ_Plane004]
  ExternalGeometry = -> [Binder008]
  FullyConstrained = true
  MakeInternals = false
  MapMode = 5
  Placement = pos=(0,0,0) rot=(1,0,0;1.5708rad)
  sketch-geometry (6):
    g0: LineSegment StartX=13.5 StartY=9 StartZ=0 EndX=17 EndY=12.5 EndZ=0
    g1: ArcOfCircle CenterX=17.5 CenterY=13 CenterZ=0 NormalX=0 NormalY=0 NormalZ=1 AngleXU=0 Radius=0.707107 StartAngle=2.35619 EndAngle=3.92699
    g2: LineSegment StartX=17 StartY=13.5 StartZ=0 EndX=13.5 EndY=17 EndZ=0
    g3: ArcOfCircle CenterX=13.5 CenterY=13 CenterZ=0 NormalX=0 NormalY=0 NormalZ=1 AngleXU=0 Radius=4 StartAngle=1.5708 EndAngle=3.14159
    g4: LineSegment StartX=9.5 StartY=13 StartZ=0 EndX=9.5 EndY=9 EndZ=0
    g5: LineSegment StartX=9.5 StartY=9 StartZ=0 EndX=13.5 EndY=9 EndZ=0
  constraints (18):
    c: Perpendicular(g0,g1) = 4.71239
    c: Coincident(g1,g2)
    c: Coincident(g3,g2)
    c: PointOnObject(g1,g2)
    c: Equal(g2,g0)
    c: PointOnObject(g0,g-4)
    c: Vertical(g2,g0)
    c: Horizontal(g-3,g0)
    c: Distance(g1,g0) = 1
    c: DistanceY(g0,g2) = 8
    c: Symmetric(g2,g0,g3)
    c: Horizontal(g3,g3)
    c: Coincident(g3,g4)
    c: PointOnObject(g4,g-3)
    c: Vertical(g4)
    c: Coincident(g4,g5)
    c: Coincident(g5,g0)
    c: Angle(g5,g0) = 0.785398
FEATURE [PartDesign::Pad] Pad005  label="RackExtrusion"
  Direction = (0,-1,2e-16)
  Length = 310
  Length2 = 10
  Midplane = true
  Placement = pos=(0,0,0) rot=(1,0,0;1.5708rad)
  Profile = -> Sketch012
  ReferenceAxis = -> Sketch012 [N_Axis]
  Refine = true
  Suppressed = false
  Type = 0
FEATURE [PartDesign::SubShapeBinder] Binder009
  BindCopyOnChange = 0
  BindMode = 0
  ClaimChildren = false
  Context = -> Body004 [Binder009.]
  Fuse = false
  MakeFace = true
  OffsetFill = false
  OffsetIntersection = false
  OffsetJoinType = 0
  OffsetOpenResult = false
  PartialLoad = false
  Refine = true
  Relative = true
  Support = -> [Body001[Sketch004.]]
  _Version = 2
FEATURE [Sketcher::SketchObject] Sketch015
  ArcFitTolerance = 1e-06
  AttachmentSupport = -> [XZ_Plane004]
  ExternalGeometry = -> [Pad005,Binder008]
  FullyConstrained = true
  MakeInternals = false
  MapMode = 5
  Placement = pos=(0,0,0) rot=(1,0,0;1.5708rad)
  sketch-geometry (4):
    g0: LineSegment StartX=6 StartY=16.5 StartZ=0 EndX=6 EndY=9 EndZ=0
    g1: LineSegment StartX=6 StartY=9 StartZ=0 EndX=13.5 EndY=9 EndZ=0
    g2: LineSegment StartX=13.5 StartY=9 StartZ=0 EndX=13.5 EndY=16.5 EndZ=0
    g3: LineSegment StartX=13.5 StartY=16.5 StartZ=0 EndX=6 EndY=16.5 EndZ=0
  constraints (11):
    c: Coincident(g0,g1)
    c: Coincident(g1,g2)
    c: Coincident(g2,g3)
    c: Coincident(g3,g0)
    c: Vertical(g0)
    c: Vertical(g2)
    c: Horizontal(g1)
    c: Horizontal(g3)
    c: Coincident(g1,g-3)
    c: Vertical(g0,g-4)
    c: Distance(g0,g0) = 7.5
FEATURE [PartDesign::Pad] Pad006
  BaseFeature = -> Pad005
  Direction = (0,-1,2e-16)
  Length = 45.4
  Length2 = 10
  Midplane = true
  Placement = pos=(0,0,0) rot=(1,0,0;1.5708rad)
  Profile = -> Sketch015
  ReferenceAxis = -> Sketch015 [N_Axis]
  Refine = true
  Suppressed = false
  Type = 0
  expr: Length = <<BlockExtent>>.Length
FEATURE [Sketcher::SketchObject] Sketch016
  ArcFitTolerance = 1e-06
  AttachmentSupport = -> [Pad006]
  ExternalGeometry = -> [Binder009]
  FullyConstrained = true
  MakeInternals = false
  MapMode = 5
  Placement = pos=(0,7.3e-15,16.5) rot=(0,0,1;3.14159rad)
  sketch-geometry (2):
    g0: Circle CenterX=-10 CenterY=10 CenterZ=0 NormalX=0 NormalY=0 NormalZ=1 AngleXU=0 Radius=2.23133
    g1: Circle CenterX=-10 CenterY=-10 CenterZ=0 NormalX=0 NormalY=0 NormalZ=1 AngleXU=0 Radius=2.44373
  constraints (4):
    c: Coincident(g0,g-3)
    c: Equal(g0,g-3)
    c: Coincident(g1,g-4)
    c: Equal(g1,g-4)
FEATURE [PartDesign::Hole] Hole004
  BaseFeature = -> Pad006
  CustomThreadClearance = 0
  Depth = 25
  DepthType = 0
  Diameter = 3.4
  DrillForDepth = false
  DrillPoint = 1
  DrillPointAngle = 118
  HoleCutCountersinkAngle = 90
  HoleCutCustomValues = false
  HoleCutDepth = 2
  HoleCutDiameter = 6.1
  HoleCutType = 1
  ModelThread = false
  Placement = pos=(0,0,0) rot=(1,0,0;1.5708rad)
  Profile = -> Sketch016
  Refine = true
  Suppressed = false
  Tapered = false
  TaperedAngle = 90
  ThreadClass = 0
  ThreadDepth = 25
  ThreadDepthType = 0
  ThreadDirection = 0
  ThreadFit = 0
  ThreadSize = 9
  ThreadType = 1
  Threaded = false
  UseCustomThreadClearance = false
FEATURE [Sketcher::SketchObject] Sketch017
  ArcFitTolerance = 1e-06
  AttachmentSupport = -> [Hole004]
  ExternalGeometry = -> [Hole004]
  FullyConstrained = true
  MakeInternals = false
  MapMode = 5
  Placement = pos=(0,7.3e-15,16.5) rot=(0,0,1;3.14159rad)
  sketch-geometry (2):
    g0: Circle CenterX=-10 CenterY=10 CenterZ=0 NormalX=0 NormalY=0 NormalZ=1 AngleXU=0 Radius=3.05
    g1: Circle CenterX=-10 CenterY=-10 CenterZ=0 NormalX=0 NormalY=0 NormalZ=1 AngleXU=0 Radius=3.05
  constraints (4):
    c: Coincident(g0,g-3)
    c: Equal(g0,g-3)
    c: Coincident(g1,g-4)
    c: Equal(g1,g-4)
FEATURE [PartDesign::Pocket] Pocket002
  BaseFeature = -> Hole004
  Direction = (0,0,-1)
  Length = 5
  Length2 = 5
  Placement = pos=(0,0,0) rot=(1,0,0;1.5708rad)
  Profile = -> Sketch017
  ReferenceAxis = -> Sketch017 [N_Axis]
  Refine = true
  Reversed = true
  Suppressed = false
  Type = 1
FEATURE [Sketcher::SketchObject] Sketch018  label="RackStringEnds"
  ArcFitTolerance = 1e-06
  AttachmentSupport = -> [Pocket002]
  ExternalGeometry = -> [Pocket002]
  FullyConstrained = true
  MakeInternals = false
  MapMode = 5
  Placement = pos=(9.5,0,0) rot=(0.707107,0,-0.707107;3.14159rad)
  sketch-geometry (3):
    g0: Circle CenterX=-13 CenterY=150 CenterZ=0 NormalX=0 NormalY=0 NormalZ=1 AngleXU=0 Radius=0.75
    g1: Circle CenterX=-13 CenterY=-150 CenterZ=0 NormalX=0 NormalY=0 NormalZ=1 AngleXU=0 Radius=0.75
    g2: GeomPoint [constr] X=-13 Y=-155 Z=0
  constraints (6):
    c: Symmetric(g1,g0,g-1)
    c: Equal(g0,g1)
    c: Symmetric(g-4,g-3,g2)
    c: Vertical(g2,g1)
    c: Diameter(g1) = 1.5  'stringHoleDiameter'
    c: DistanceY(g1,g0) = 300  'Length'
FEATURE [PartDesign::Pocket] Pocket003
  BaseFeature = -> Pocket002
  Direction = (1,0,2e-16)
  Length = 5
  Length2 = 5
  Placement = pos=(0,0,0) rot=(1,0,0;1.5708rad)
  Profile = -> Sketch018
  ReferenceAxis = -> Sketch018 [N_Axis]
  Refine = true
  Suppressed = false
  Type = 1
FEATURE [PartDesign::Fillet] Fillet
  Base = -> Pocket003 [Edge59,Edge62]
  BaseFeature = -> Pocket003
  Placement = pos=(0,0,0) rot=(1,0,0;1.5708rad)
  Radius = 3
  Refine = true
  SupportTransform = false
  Suppressed = false
  UseAllEdges = false
FEATURE [PartDesign::Body] Body004  label="Rack"
  AllowCompound = false
  Group = -> [Binder008,Sketch012,Pad005,Binder009,Sketch015,Pad006,Sketch016,Hole004,Sketch017,Pocket002,Sketch018,Pocket003,Fillet]
  Origin = -> Origin004
  Tip = -> Fillet
COMPONENT P10 — recipe-attached ("Rail001", modeled in this document).
Construction recipe (the document's own serialized feature program — sketch geometry with constraints, then the solid features built on it; lengths are millimeters unless a unit is written):

FEATURE [Sketcher::SketchObject] Sketch  label="Rail Cross-Section"
  ArcFitTolerance = 1e-06
  AttachmentSupport = -> [XZ_Plane]
  FullyConstrained = true
  MakeInternals = false
  MapMode = 5
  Placement = pos=(0,0,0) rot=(1,0,0;1.5708rad)
  sketch-geometry (11):
    g0: LineSegment StartX=-6 StartY=4 StartZ=0 EndX=-6 EndY=-3.35 EndZ=0
    g1: LineSegment StartX=-5.35 StartY=-4 StartZ=0 EndX=5.35 EndY=-4 EndZ=0
    g2: LineSegment StartX=6 StartY=-3.35 StartZ=0 EndX=6 EndY=4 EndZ=0
    g3: LineSegment StartX=6 StartY=4 StartZ=0 EndX=-6 EndY=4 EndZ=0
    g4: GeomPoint [constr] X=0 Y=0 Z=0
    g5: GeomPoint [constr] X=-6 Y=4 Z=0
    g6: GeomPoint [constr] X=6 Y=4 Z=0
    g7: ArcOfCircle CenterX=5.35 CenterY=-3.35 CenterZ=0 NormalX=0 NormalY=0 NormalZ=1 AngleXU=0 Radius=0.65 StartAngle=4.71239 EndAngle=6.28319
    g8: GeomPoint [constr] X=6 Y=-4 Z=0
    g9: ArcOfCircle CenterX=-5.35 CenterY=-3.35 CenterZ=0 NormalX=0 NormalY=0 NormalZ=1 AngleXU=0 Radius=0.65 StartAngle=3.14159 EndAngle=4.71239
    g10: GeomPoint [constr] X=-6 Y=-4 Z=0
  constraints (22):
    c: Vertical(g0)
    c: Vertical(g2)
    c: Horizontal(g1)
    c: Horizontal(g3)
    c: Symmetric(g8,g5,g4)
    c: Coincident(g4,g-1)
    c: DistanceX(g5,g6) = 12  'Wr'
    c: DistanceY(g8,g6) = 8  'Hr'
    c: PointOnObject(g8,g2)
    c: PointOnObject(g8,g1)
    c: Tangent(g2,g7) = -1.5708
    c: Tangent(g1,g7) = -1.5708
    c: PointOnObject(g10,g1)
    c: PointOnObject(g10,g0)
    c: Tangent(g1,g9) = -1.5708
    c: Tangent(g0,g9) = -1.5708
    c: Equal(g9,g7)
    c: Coincident(g2,g6)
    c: Coincident(g3,g2)
    c: Coincident(g0,g5)
    c: Coincident(g3,g0)
    c: Radius(g9) = 0.65  'radius'
FEATURE [PartDesign::Pad] Pad  label="Rail Extrusion"
  Direction = (0,-1,2e-16)
  Length = 600
  Length2 = 10
  Midplane = true
  Placement = pos=(0,0,0) rot=(1,0,0;1.5708rad)
  Profile = -> Sketch
  ReferenceAxis = -> Sketch [N_Axis]
  Refine = true
  Suppressed = false
  Type = 0
FEATURE [Sketcher::SketchObject] Sketch005  label="RailHolePosition"
  ArcFitTolerance = 1e-06
  AttachmentSupport = -> [Pad]
  ExternalGeometry = -> [Pad]
  FullyConstrained = false
  MakeInternals = false
  MapMode = 5
  Placement = pos=(0,1.8e-15,4) rot=(0,0,1;3.14159rad)
  sketch-geometry (1):
    g0: Circle CenterX=0 CenterY=-287.5 CenterZ=0 NormalX=0 NormalY=0 NormalZ=1 AngleXU=0 Radius=2.44176
  constraints (2):
    c: PointOnObject(g0,g-2)
    c: DistanceY(g-3,g0) = 12.5  'E'
FEATURE [PartDesign::Hole] Hole001
  BaseFeature = -> Pad
  CustomThreadClearance = 0
  Depth = 1212.35
  DepthType = 1
  Diameter = 3.4
  DrillForDepth = false
  DrillPoint = 1
  DrillPointAngle = 118
  HoleCutCountersinkAngle = 90
  HoleCutCustomValues = false
  HoleCutDepth = 3.4
  HoleCutDiameter = 6.1
  HoleCutType = 1
  ModelThread = false
  Placement = pos=(0,0,0) rot=(1,0,0;1.5708rad)
  Profile = -> Sketch005
  Refine = true
  Suppressed = false
  Tapered = false
  TaperedAngle = 90
  ThreadClass = 0
  ThreadDepth = 1212.35
  ThreadDepthType = 0
  ThreadDirection = 0
  ThreadFit = 0
  ThreadSize = 9
  ThreadType = 1
  Threaded = false
  UseCustomThreadClearance = false
FEATURE [PartDesign::LinearPattern] LinearPattern
  BaseFeature = -> Hole001
  Direction = -> Y_Axis
  Length = 575
  Mode = 1
  Occurrences = 24
  Offset = 25
  Originals = -> [Hole001]
  Placement = pos=(0,0,0) rot=(1,0,0;1.5708rad)
  Refine = true
  Reversed = true
  Suppressed = false
  TransformMode = 0
  expr: Occurrences = <<Rail Extrusion>>.Length / 25
FEATURE [PartDesign::Body] Body  label="Rail"
  AllowCompound = false
  Group = -> [Sketch,Pad,Sketch005,Hole001,LinearPattern]
  Origin = -> Origin
  Tip = -> LinearPattern
COMPONENT P11 — recipe-attached ("Servo001", modeled in this document).
Construction recipe (the document's own serialized feature program — sketch geometry with constraints, then the solid features built on it; lengths are millimeters unless a unit is written):

FEATURE [PartDesign::SubShapeBinder] Binder014
  BindCopyOnChange = 0
  BindMode = 0
  ClaimChildren = false
  Context = -> Body007 [Binder014.]
  Fuse = false
  MakeFace = true
  OffsetFill = false
  OffsetIntersection = false
  OffsetJoinType = 0
  OffsetOpenResult = false
  PartialLoad = false
  Refine = true
  Relative = true
  Support = -> [Body005[Sketch019.]]
  _Version = 2
FEATURE [Sketcher::SketchObject] Sketch029
  ArcFitTolerance = 1e-06
  AttachmentSupport = -> [XZ_Plane008]
  ExternalGeometry = -> [Binder014]
  FullyConstrained = true
  MakeInternals = false
  MapMode = 5
  Placement = pos=(0,0,0) rot=(1,0,0;1.5708rad)
  expr: Constraints[12] = <<PinionCrossSection>>.Constraints.ServoBodyHeight
  expr: Constraints[13] = <<PinionCrossSection>>.Constraints.ServoBodyWidth
  expr: Constraints[2] = <<PinionCrossSection>>.Constraints.ServoShaftLength
  sketch-geometry (5):
    g0: LineSegment [constr] StartX=112.51 StartY=31.9532 StartZ=0 EndX=113.539 EndY=27.0602 EndZ=0
    g1: LineSegment StartX=104.732 StartY=25.2077 StartZ=0 EndX=122.347 EndY=28.9128 EndZ=0
    g2: LineSegment StartX=122.347 StartY=28.9128 StartZ=0 EndX=129.963 EndY=-7.29486 EndZ=0
    g3: LineSegment StartX=129.963 StartY=-7.29486 StartZ=0 EndX=112.348 EndY=-11 EndZ=0
    g4: LineSegment StartX=112.348 StartY=-11 StartZ=0 EndX=104.732 EndY=25.2077 EndZ=0
  constraints (14):
    c: Coincident(g0,g-3)
    c: PointOnObject(g-3,g0)
    c: Distance(g0,g0) = 5
    c: Coincident(g1,g2)
    c: Coincident(g2,g3)
    c: Coincident(g3,g4)
    c: Coincident(g4,g1)
    c: Perpendicular(g1,g4)
    c: Perpendicular(g2,g1)
    c: Perpendicular(g3,g2)
    c: Parallel(g0,g2)
    c: Symmetric(g1,g1,g0)
    c: Distance(g2,g2) = 37
    c: Distance(g3,g3) = 18
FEATURE [PartDesign::Pad] Pad010
  Direction = (0,-1,2e-16)
  Length = 39
  Length2 = 10
  Midplane = true
  Placement = pos=(0,0,0) rot=(1,0,0;1.5708rad)
  Profile = -> Sketch029
  ReferenceAxis = -> Sketch029 [N_Axis]
  Refine = true
  Suppressed = false
  Type = 0
  expr: Length = <<ServoCutout>>.Constraints.ServoDepth
FEATURE [Sketcher::SketchObject] Sketch030
  ArcFitTolerance = 1e-06
  AttachmentSupport = -> [XZ_Plane008]
  ExternalGeometry = -> [Pad010]
  FullyConstrained = true
  MakeInternals = false
  MapMode = 5
  Placement = pos=(0,0,0) rot=(1,0,0;1.5708rad)
  expr: Constraints[10] = <<StandCrossSection>>.Constraints.ServoFlangeThickness
  expr: Constraints[11] = <<StandCrossSection>>.Constraints.ServoUnderFlangeHeight
  sketch-geometry (4):
    g0: LineSegment StartX=106.688 StartY=15.9111 StartZ=0 EndX=107.202 EndY=13.4646 EndZ=0
    g1: LineSegment StartX=107.202 StartY=13.4646 StartZ=0 EndX=124.817 EndY=17.1698 EndZ=0
    g2: LineSegment StartX=124.817 StartY=17.1698 StartZ=0 EndX=124.302 EndY=19.6162 EndZ=0
    g3: LineSegment StartX=124.302 StartY=19.6162 StartZ=0 EndX=106.688 EndY=15.9111 EndZ=0
  constraints (12):
    c: PointOnObject(g0,g-3)
    c: PointOnObject(g0,g-3)
    c: Coincident(g0,g1)
    c: PointOnObject(g1,g-4)
    c: Coincident(g1,g2)
    c: PointOnObject(g2,g-4)
    c: Coincident(g2,g3)
    c: Coincident(g3,g0)
    c: Perpendicular(g3,g-3)
    c: Perpendicular(g1,g-3)
    c: Distance(g2,g2) = 2.5
    c: Distance(g1,g-4) = 25
FEATURE [PartDesign::Pad] Pad011
  BaseFeature = -> Pad010
  Direction = (0,-1,2e-16)
  Length = 55
  Length2 = 10
  Midplane = true
  Placement = pos=(0,0,0) rot=(1,0,0;1.5708rad)
  Profile = -> Sketch030
  ReferenceAxis = -> Sketch030 [N_Axis]
  Refine = true
  Suppressed = false
  Type = 0
FEATURE [Sketcher::SketchObject] Sketch031
  ArcFitTolerance = 1e-06
  AttachmentSupport = -> [Pad011]
  ExternalGeometry = -> [Pad011]
  FullyConstrained = true
  MakeInternals = false
  MapMode = 5
  Placement = pos=(-0.640095,1.3e-15,3.04306) rot=(-0.103476,0,0.994632;3.14159rad)
  expr: Constraints[1] = <<PinionServoMountingHoles>>.Constraints.ServoShaftDiameter
  sketch-geometry (1):
    g0: Circle CenterX=-116.678 CenterY=-3.2e-15 CenterZ=0 NormalX=0 NormalY=0 NormalZ=1 AngleXU=0 Radius=4
  constraints (2):
    c: Symmetric(g-3,g-4,g0)
    c: Diameter(g0) = 8
FEATURE [PartDesign::Pad] Pad012
  BaseFeature = -> Pad011
  Direction = (-0.205841,0,0.978585)
  Length = 5
  Length2 = 10
  Placement = pos=(0,0,0) rot=(1,0,0;1.5708rad)
  Profile = -> Sketch031
  ReferenceAxis = -> Sketch031 [N_Axis]
  Refine = true
  Suppressed = false
  Type = 0
  expr: Length = <<PinionCrossSection>>.Constraints.ServoShaftLength
FEATURE [PartDesign::SubShapeBinder] Binder015
  BindCopyOnChange = 0
  BindMode = 0
  ClaimChildren = false
  Context = -> Body007 [Binder015.]
  Fuse = false
  MakeFace = true
  OffsetFill = false
  OffsetIntersection = false
  OffsetJoinType = 0
  OffsetOpenResult = false
  PartialLoad = false
  Refine = true
  Relative = true
  Support = -> [Body006[Pocket007.Edge105,Pocket007.Edge104,Pocket007.Edge91,Pocket007.Edge92]]
  _Version = 2
FEATURE [PartDesign::Pocket] Pocket009
  BaseFeature = -> Pad012
  Direction = (0.205841,0,-0.978585)
  Length = 5
  Length2 = 5
  Placement = pos=(0,0,0) rot=(1,0,0;1.5708rad)
  Profile = -> Binder015
  Refine = true
  Reversed = true
  Suppressed = false
  Type = 1
FEATURE [PartDesign::Body] Body007  label="Servo"
  AllowCompound = false
  Group = -> [Binder014,Sketch029,Pad010,Sketch030,Pad011,Sketch031,Pad012,Binder015,Pocket009]
  Origin = -> Origin008
  Tip = -> Pocket009
